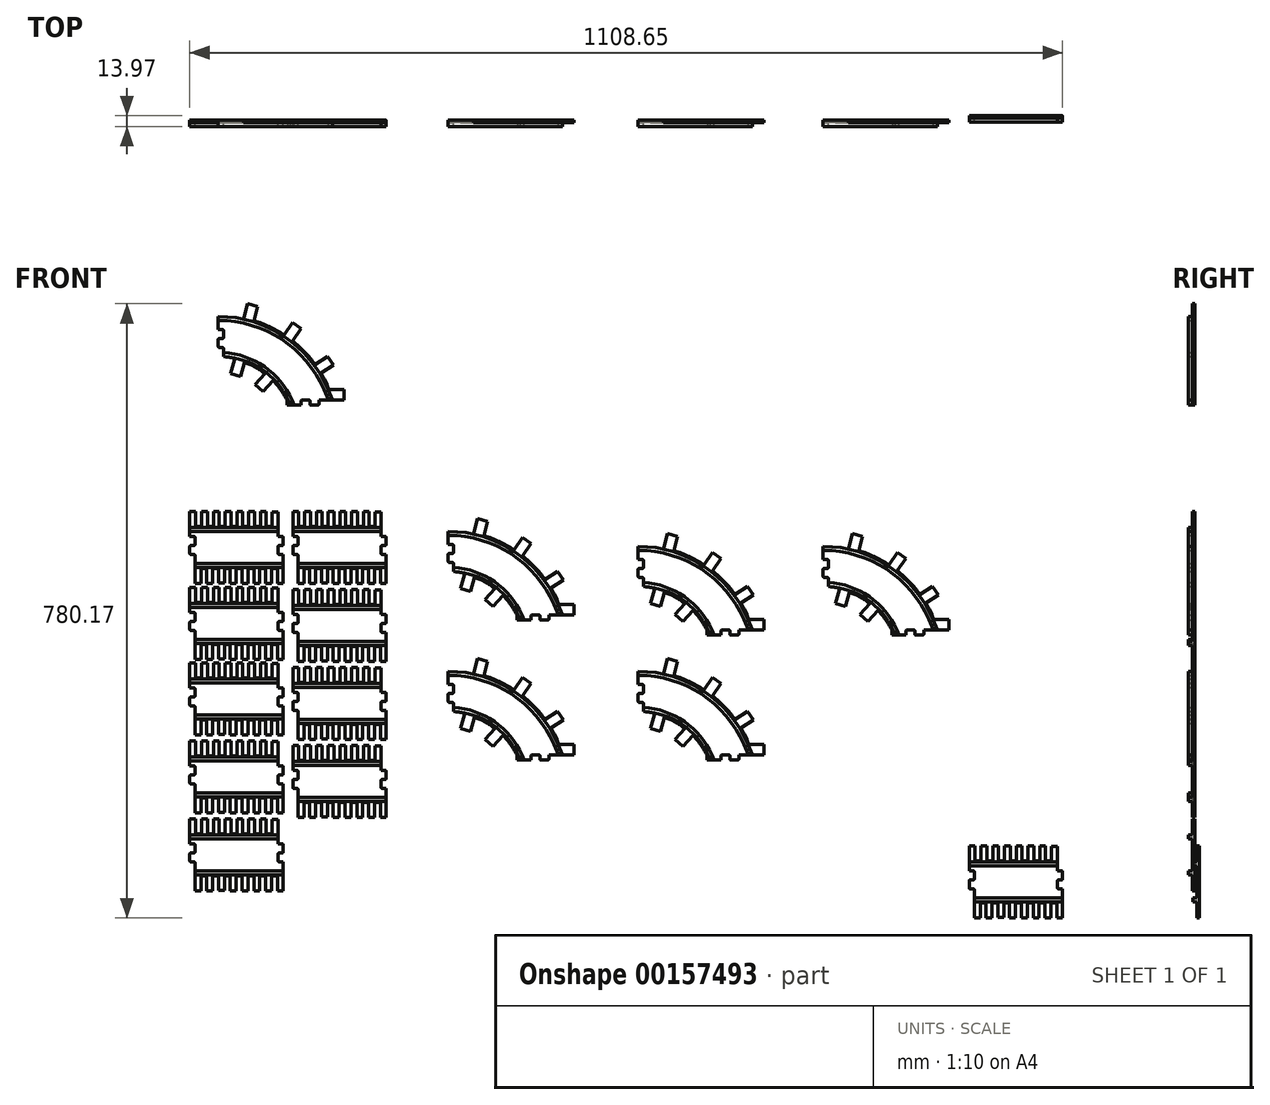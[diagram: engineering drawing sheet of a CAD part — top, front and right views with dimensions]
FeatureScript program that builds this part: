
annotation { "Feature Type Name" : "Feature", "Feature Type Description" : "" }
export const myFeature = defineFeature(function(context is Context, id is Id, definition is map)
    precondition{}
    {
        {
            var Q0;
            Q0=qCreatedBy(makeId("Front.planeOp"),FACE);
            var sketch = newSketch(context, id + "F0", { "sketchPlane" : qUnion([Q0])});
            skLineSegment(sketch, "E0.bottom", {"start": v(-84.07, 34.3) * mm, "end": v(26.8, 34.3) * mm});
            skLineSegment(sketch, "E0.top", {"start": v(-84.07, 29.2) * mm, "end": v(26.8, 29.2) * mm});
            skLineSegment(sketch, "E0.right", {"start": v(26.8, 34.29) * mm, "end": v(26.8, 29.2) * mm});
            skLineSegment(sketch, "E1", {"start": v(-78.78, 21.6) * mm, "end": v(-78.78, 12.7) * mm});
            skLineSegment(sketch, "E2", {"start": v(-80.05, 11.43) * mm, "end": v(-84.06, 11.43) * mm});
            skLineSegment(sketch, "E3", {"start": v(-85.33, 10.16) * mm, "end": v(-85.33, 1.27) * mm});
            skLineSegment(sketch, "E4", {"start": v(-84.06, 0) * mm, "end": v(-80.05, 0) * mm});
            skLineSegment(sketch, "E5", {"start": v(-78.78, -1.27) * mm, "end": v(-78.78, -11.43) * mm});
            skPoint(sketch, "E6.visualSharp", {"position": v(-78.78, 22.86) * mm});
            skArc(sketch, "E6.filletArc", {"start": v(-78.78, 21.6) * mm, "mid": v(-79.15, 22.49) * mm, "end": v(-80.05, 22.86) * mm});
            skPoint(sketch, "E7.visualSharp", {"position": v(-78.78, 11.43) * mm});
            skArc(sketch, "E7.filletArc", {"start": v(-80.05, 11.43) * mm, "mid": v(-79.15, 11.8) * mm, "end": v(-78.78, 12.7) * mm});
            skPoint(sketch, "E8.visualSharp", {"position": v(-85.33, 11.43) * mm});
            skArc(sketch, "E8.filletArc", {"start": v(-84.06, 11.43) * mm, "mid": v(-84.96, 11.06) * mm, "end": v(-85.33, 10.16) * mm});
            skPoint(sketch, "E9.visualSharp", {"position": v(-85.33, 0) * mm});
            skArc(sketch, "E9.filletArc", {"start": v(-85.33, 1.27) * mm, "mid": v(-84.96, 0.37) * mm, "end": v(-84.06, 0) * mm});
            skPoint(sketch, "E10.visualSharp", {"position": v(-78.78, 0) * mm});
            skArc(sketch, "E10.filletArc", {"start": v(-78.78, -1.27) * mm, "mid": v(-79.15, -0.37) * mm, "end": v(-80.05, 0) * mm});
            skLineSegment(sketch, "E11", {"start": v(26.8, 29.2) * mm, "end": v(26.8, 22.86) * mm});
            skLineSegment(sketch, "E12", {"start": v(26.8, 22.86) * mm, "end": v(32.09, 22.86) * mm});
            skLineSegment(sketch, "E13", {"start": v(-78.78, -11.43) * mm, "end": v(32.39, -11.43) * mm});
            skPoint(sketch, "E14.visualSharp", {"position": v(33.36, 22.86) * mm});
            skPoint(sketch, "E15.visualSharp", {"position": v(44.08, 6.35) * mm});
            skPoint(sketch, "E16.visualSharp", {"position": v(33.84, 11.43) * mm});
            skPoint(sketch, "E17.visualSharp", {"position": v(33.84, 0) * mm});
            skArc(sketch, "E17.filletArc", {"start": v(26.8, 1.27) * mm, "mid": v(27.18, 0.37) * mm, "end": v(28.07, 0) * mm});
            skLineSegment(sketch, "E18.left", {"start": v(-78.78, -11.43) * mm, "end": v(-78.78, -16.51) * mm});
            skLineSegment(sketch, "E19", {"start": v(33.36, 21.59) * mm, "end": v(33.36, 12.7) * mm});
            skLineSegment(sketch, "E20", {"start": v(32.09, 11.43) * mm, "end": v(28.07, 11.43) * mm});
            skArc(sketch, "E21.filletArc", {"start": v(33.36, 21.59) * mm, "mid": v(32.99, 22.49) * mm, "end": v(32.09, 22.86) * mm});
            skPoint(sketch, "E22.visualSharp", {"position": v(33.36, 11.43) * mm});
            skArc(sketch, "E22.filletArc", {"start": v(32.09, 11.43) * mm, "mid": v(32.99, 11.8) * mm, "end": v(33.36, 12.7) * mm});
            skLineSegment(sketch, "E23", {"start": v(26.8, 1.27) * mm, "end": v(26.8, 10.16) * mm});
            skPoint(sketch, "E24.visualSharp", {"position": v(26.8, 11.43) * mm});
            skArc(sketch, "E24.filletArc", {"start": v(28.07, 11.43) * mm, "mid": v(27.18, 11.06) * mm, "end": v(26.8, 10.16) * mm});
            skLineSegment(sketch, "E25", {"start": v(-85.34, 54.61) * mm, "end": v(-77.87, 54.61) * mm});
            skLineSegment(sketch, "E26", {"start": v(-77.87, 54.61) * mm, "end": v(-77.87, 35.74) * mm});
            skLineSegment(sketch, "E27", {"start": v(-77.87, 35.74) * mm, "end": v(-70.4, 35.74) * mm});
            skLineSegment(sketch, "E28", {"start": v(-70.4, 35.74) * mm, "end": v(-70.4, 54.6) * mm});
            skLineSegment(sketch, "E29", {"start": v(-70.4, 54.61) * mm, "end": v(-62.93, 54.61) * mm});
            skLineSegment(sketch, "E30", {"start": v(-62.93, 54.6) * mm, "end": v(-62.93, 35.74) * mm});
            skLineSegment(sketch, "E31", {"start": v(-62.93, 35.74) * mm, "end": v(-55.46, 35.74) * mm});
            skLineSegment(sketch, "E32", {"start": v(-55.46, 35.74) * mm, "end": v(-55.46, 54.6) * mm});
            skLineSegment(sketch, "E33", {"start": v(-55.46, 54.61) * mm, "end": v(-48, 54.61) * mm});
            skLineSegment(sketch, "E34", {"start": v(-48, 54.6) * mm, "end": v(-48, 35.74) * mm});
            skLineSegment(sketch, "E35", {"start": v(-48, 35.74) * mm, "end": v(-40.52, 35.74) * mm});
            skLineSegment(sketch, "E36", {"start": v(-40.52, 35.74) * mm, "end": v(-40.52, 54.6) * mm});
            skLineSegment(sketch, "E37", {"start": v(-40.52, 54.61) * mm, "end": v(-33.05, 54.61) * mm});
            skLineSegment(sketch, "E38", {"start": v(-33.05, 54.6) * mm, "end": v(-33.05, 35.74) * mm});
            skLineSegment(sketch, "E39", {"start": v(-33.05, 35.74) * mm, "end": v(-25.58, 35.74) * mm});
            skLineSegment(sketch, "E40", {"start": v(-25.58, 35.74) * mm, "end": v(-25.58, 54.6) * mm});
            skLineSegment(sketch, "E41", {"start": v(-25.58, 54.61) * mm, "end": v(-18.11, 54.61) * mm});
            skLineSegment(sketch, "E42", {"start": v(-18.11, 54.6) * mm, "end": v(-18.11, 35.74) * mm});
            skLineSegment(sketch, "E43", {"start": v(-18.11, 35.74) * mm, "end": v(-10.64, 35.74) * mm});
            skLineSegment(sketch, "E44", {"start": v(-10.64, 35.74) * mm, "end": v(-10.64, 54.6) * mm});
            skLineSegment(sketch, "E45", {"start": v(-10.64, 54.61) * mm, "end": v(-3.18, 54.61) * mm});
            skLineSegment(sketch, "E46", {"start": v(-3.18, 54.6) * mm, "end": v(-3.18, 35.74) * mm});
            skLineSegment(sketch, "E47", {"start": v(-3.18, 35.74) * mm, "end": v(4.3, 35.74) * mm});
            skLineSegment(sketch, "E48", {"start": v(4.3, 35.74) * mm, "end": v(4.3, 54.6) * mm});
            skLineSegment(sketch, "E49", {"start": v(4.3, 54.61) * mm, "end": v(11.76, 54.61) * mm});
            skLineSegment(sketch, "E50", {"start": v(11.76, 54.6) * mm, "end": v(11.76, 35.74) * mm});
            skLineSegment(sketch, "E51", {"start": v(11.76, 35.74) * mm, "end": v(19.23, 35.74) * mm});
            skLineSegment(sketch, "E52", {"start": v(19.23, 35.74) * mm, "end": v(19.23, 54.27) * mm});
            skLineSegment(sketch, "E53", {"start": v(19.23, 54.27) * mm, "end": v(26.7, 54.27) * mm});
            skLineSegment(sketch, "E54", {"start": v(26.8, 34.29) * mm, "end": v(26.7, 54.27) * mm});
            skLineSegment(sketch, "E55", {"start": v(-84.06, 22.86) * mm, "end": v(-80.05, 22.86) * mm});
            skLineSegment(sketch, "E56", {"start": v(28.07, 0) * mm, "end": v(33.36, 0) * mm});
            skLineSegment(sketch, "E57", {"start": v(33.36, 0) * mm, "end": v(33.36, -11.43) * mm});
            skLineSegment(sketch, "E58", {"start": v(32.39, -11.43) * mm, "end": v(33.36, -11.43) * mm});
            skLineSegment(sketch, "E59", {"start": v(33.36, -11.43) * mm, "end": v(33.36, -16.51) * mm});
            skLineSegment(sketch, "E60", {"start": v(-78.78, -16.51) * mm, "end": v(33.36, -16.5) * mm});
            skLineSegment(sketch, "E61", {"start": v(-78.78, 11.43) * mm, "end": v(33.84, 11.43) * mm});
            skLineSegment(sketch, "E62", {"start": v(33.36, -16.51) * mm, "end": v(33.36, -36.83) * mm});
            skLineSegment(sketch, "E63", {"start": v(33.36, -36.83) * mm, "end": v(25.89, -36.83) * mm});
            skLineSegment(sketch, "E64", {"start": v(25.89, -36.83) * mm, "end": v(25.89, -17.96) * mm});
            skLineSegment(sketch, "E65", {"start": v(25.89, -17.96) * mm, "end": v(18.42, -17.96) * mm});
            skLineSegment(sketch, "E66", {"start": v(18.42, -17.96) * mm, "end": v(18.42, -36.83) * mm});
            skLineSegment(sketch, "E67", {"start": v(18.42, -36.83) * mm, "end": v(10.95, -36.83) * mm});
            skLineSegment(sketch, "E68", {"start": v(10.95, -36.83) * mm, "end": v(10.95, -17.96) * mm});
            skLineSegment(sketch, "E69", {"start": v(10.95, -17.96) * mm, "end": v(3.48, -17.96) * mm});
            skLineSegment(sketch, "E70", {"start": v(3.48, -17.96) * mm, "end": v(3.48, -36.83) * mm});
            skLineSegment(sketch, "E71", {"start": v(3.48, -36.83) * mm, "end": v(-3.99, -36.83) * mm});
            skLineSegment(sketch, "E72", {"start": v(-3.99, -36.83) * mm, "end": v(-3.99, -17.96) * mm});
            skLineSegment(sketch, "E73", {"start": v(-3.99, -17.96) * mm, "end": v(-11.55, -17.96) * mm});
            skLineSegment(sketch, "E74", {"start": v(-11.55, -17.96) * mm, "end": v(-11.55, -36.83) * mm});
            skLineSegment(sketch, "E75", {"start": v(-11.55, -36.83) * mm, "end": v(-19.02, -36.83) * mm});
            skLineSegment(sketch, "E76", {"start": v(-19.02, -36.83) * mm, "end": v(-19.02, -17.96) * mm});
            skLineSegment(sketch, "E77", {"start": v(-19.02, -17.96) * mm, "end": v(-26.5, -17.96) * mm});
            skLineSegment(sketch, "E78", {"start": v(-26.5, -17.96) * mm, "end": v(-26.5, -36.83) * mm});
            skLineSegment(sketch, "E79", {"start": v(-26.5, -36.83) * mm, "end": v(-33.96, -36.83) * mm});
            skLineSegment(sketch, "E80", {"start": v(-33.96, -36.83) * mm, "end": v(-33.96, -17.96) * mm});
            skLineSegment(sketch, "E81", {"start": v(-33.96, -17.96) * mm, "end": v(-41.43, -17.96) * mm});
            skLineSegment(sketch, "E82", {"start": v(-41.43, -17.96) * mm, "end": v(-41.43, -36.12) * mm});
            skLineSegment(sketch, "E83", {"start": v(-41.43, -36.12) * mm, "end": v(-48.9, -36.12) * mm});
            skLineSegment(sketch, "E84", {"start": v(-48.9, -36.12) * mm, "end": v(-48.9, -17.96) * mm});
            skLineSegment(sketch, "E85", {"start": v(-48.9, -17.96) * mm, "end": v(-56.37, -17.96) * mm});
            skLineSegment(sketch, "E86", {"start": v(-56.37, -17.96) * mm, "end": v(-56.37, -36.83) * mm});
            skLineSegment(sketch, "E87", {"start": v(-56.37, -36.83) * mm, "end": v(-63.84, -36.83) * mm});
            skLineSegment(sketch, "E88", {"start": v(-63.84, -36.83) * mm, "end": v(-63.84, -17.96) * mm});
            skLineSegment(sketch, "E89", {"start": v(-63.84, -17.96) * mm, "end": v(-71.3, -17.96) * mm});
            skLineSegment(sketch, "E90", {"start": v(-71.3, -17.96) * mm, "end": v(-71.3, -36.6) * mm});
            skLineSegment(sketch, "E91", {"start": v(-71.3, -36.6) * mm, "end": v(-76.52, -36.6) * mm});
            skLineSegment(sketch, "E92", {"start": v(-78.78, -16.51) * mm, "end": v(-78.78, -36.63) * mm});
            skLineSegment(sketch, "E93", {"start": v(-78.78, -36.63) * mm, "end": v(-76.52, -36.6) * mm});
            skLineSegment(sketch, "E94", {"start": v(-84.06, 22.86) * mm, "end": v(-85.33, 22.86) * mm});
            skLineSegment(sketch, "E95", {"start": v(-85.33, 22.86) * mm, "end": v(-85.33, 22.82) * mm});
            skLineSegment(sketch, "E96", {"start": v(-85.33, 22.86) * mm, "end": v(-85.33, 29.23) * mm});
            skLineSegment(sketch, "E97", {"start": v(-84.07, 29.2) * mm, "end": v(-85.33, 29.2) * mm});
            skLineSegment(sketch, "E98", {"start": v(-85.33, 54.61) * mm, "end": v(-85.34, 54.61) * mm});
            skLineSegment(sketch, "E99", {"start": v(-85.33, 29.23) * mm, "end": v(-85.33, 54.61) * mm});
            skLineSegment(sketch, "E100", {"start": v(-84.07, 34.3) * mm, "end": v(-85.33, 34.29) * mm});
            skSolve(sketch);
        }
        {
            var Q0;
            Q0 = qSketchRegion(id + "F0", true);
            extrude(context, id + "F1", {"entities" : qUnion([Q0]), "depth" : 3.17 * mm});
        }
        {
            var Q0;
            Q0=makeQuery(id+"F1.opExtrude","CAP_FACE",FACE,{"disambiguationData":[OSD([sQuery(id+"F0.wireOp",EDGE,"E0.right"),sQuery(id+"F0.wireOp",EDGE,"E1"),sQuery(id+"F0.wireOp",EDGE,"E2"),sQuery(id+"F0.wireOp",EDGE,"E3"),sQuery(id+"F0.wireOp",EDGE,"E4"),sQuery(id+"F0.wireOp",EDGE,"E5"),sQuery(id+"F0.wireOp",EDGE,"E6.filletArc"),sQuery(id+"F0.wireOp",EDGE,"E7.filletArc"),sQuery(id+"F0.wireOp",EDGE,"E8.filletArc"),sQuery(id+"F0.wireOp",EDGE,"E9.filletArc"),sQuery(id+"F0.wireOp",EDGE,"E10.filletArc"),sQuery(id+"F0.wireOp",EDGE,"E11"),sQuery(id+"F0.wireOp",EDGE,"E17.filletArc"),sQuery(id+"F0.wireOp",EDGE,"E18.left"),sQuery(id+"F0.wireOp",EDGE,"E12"),sQuery(id+"F0.wireOp",EDGE,"E19"),sQuery(id+"F0.wireOp",EDGE,"E21.filletArc"),sQuery(id+"F0.wireOp",EDGE,"E22.filletArc"),sQuery(id+"F0.wireOp",EDGE,"E23"),sQuery(id+"F0.wireOp",EDGE,"E24.filletArc"),sQuery(id+"F0.wireOp",EDGE,"E25"),sQuery(id+"F0.wireOp",EDGE,"E26"),sQuery(id+"F0.wireOp",EDGE,"E27"),sQuery(id+"F0.wireOp",EDGE,"E28"),sQuery(id+"F0.wireOp",EDGE,"E29"),sQuery(id+"F0.wireOp",EDGE,"E30"),sQuery(id+"F0.wireOp",EDGE,"E31"),sQuery(id+"F0.wireOp",EDGE,"E32"),sQuery(id+"F0.wireOp",EDGE,"E33"),sQuery(id+"F0.wireOp",EDGE,"E34"),sQuery(id+"F0.wireOp",EDGE,"E35"),sQuery(id+"F0.wireOp",EDGE,"E36"),sQuery(id+"F0.wireOp",EDGE,"E37"),sQuery(id+"F0.wireOp",EDGE,"E38"),sQuery(id+"F0.wireOp",EDGE,"E39"),sQuery(id+"F0.wireOp",EDGE,"E40"),sQuery(id+"F0.wireOp",EDGE,"E41"),sQuery(id+"F0.wireOp",EDGE,"E42"),sQuery(id+"F0.wireOp",EDGE,"E43"),sQuery(id+"F0.wireOp",EDGE,"E44"),sQuery(id+"F0.wireOp",EDGE,"E45"),sQuery(id+"F0.wireOp",EDGE,"E46"),sQuery(id+"F0.wireOp",EDGE,"E47"),sQuery(id+"F0.wireOp",EDGE,"E48"),sQuery(id+"F0.wireOp",EDGE,"E49"),sQuery(id+"F0.wireOp",EDGE,"E50"),sQuery(id+"F0.wireOp",EDGE,"E51"),sQuery(id+"F0.wireOp",EDGE,"E52"),sQuery(id+"F0.wireOp",EDGE,"E53"),sQuery(id+"F0.wireOp",EDGE,"E54"),sQuery(id+"F0.wireOp",EDGE,"E55"),sQuery(id+"F0.wireOp",EDGE,"E56"),sQuery(id+"F0.wireOp",EDGE,"E57"),sQuery(id+"F0.wireOp",EDGE,"E59"),sQuery(id+"F0.wireOp",EDGE,"E61"),sQuery(id+"F0.wireOp",EDGE,"E62"),sQuery(id+"F0.wireOp",EDGE,"E63"),sQuery(id+"F0.wireOp",EDGE,"E64"),sQuery(id+"F0.wireOp",EDGE,"E65"),sQuery(id+"F0.wireOp",EDGE,"E66"),sQuery(id+"F0.wireOp",EDGE,"E67"),sQuery(id+"F0.wireOp",EDGE,"E68"),sQuery(id+"F0.wireOp",EDGE,"E69"),sQuery(id+"F0.wireOp",EDGE,"E70"),sQuery(id+"F0.wireOp",EDGE,"E71"),sQuery(id+"F0.wireOp",EDGE,"E72"),sQuery(id+"F0.wireOp",EDGE,"E73"),sQuery(id+"F0.wireOp",EDGE,"E74"),sQuery(id+"F0.wireOp",EDGE,"E75"),sQuery(id+"F0.wireOp",EDGE,"E76"),sQuery(id+"F0.wireOp",EDGE,"E77"),sQuery(id+"F0.wireOp",EDGE,"E78"),sQuery(id+"F0.wireOp",EDGE,"E79"),sQuery(id+"F0.wireOp",EDGE,"E80"),sQuery(id+"F0.wireOp",EDGE,"E81"),sQuery(id+"F0.wireOp",EDGE,"E82"),sQuery(id+"F0.wireOp",EDGE,"E83"),sQuery(id+"F0.wireOp",EDGE,"E84"),sQuery(id+"F0.wireOp",EDGE,"E85"),sQuery(id+"F0.wireOp",EDGE,"E86"),sQuery(id+"F0.wireOp",EDGE,"E87"),sQuery(id+"F0.wireOp",EDGE,"E88"),sQuery(id+"F0.wireOp",EDGE,"E89"),sQuery(id+"F0.wireOp",EDGE,"E90"),sQuery(id+"F0.wireOp",EDGE,"E91"),sQuery(id+"F0.wireOp",EDGE,"E92"),sQuery(id+"F0.wireOp",EDGE,"E93"),sQuery(id+"F0.wireOp",EDGE,"E94"),sQuery(id+"F0.wireOp",EDGE,"E96"),sQuery(id+"F0.wireOp",EDGE,"E99")])],"isStart":false});
            var sketch = newSketch(context, id + "F2", { "sketchPlane" : qUnion([Q0])});
            skLineSegment(sketch, "E101.0.0", {"start": v(26.8, 34.3) * mm, "end": v(-84.07, 34.3) * mm});
            skLineSegment(sketch, "E101.0.1", {"start": v(-84.07, 34.3) * mm, "end": v(-85.33, 34.29) * mm});
            skLineSegment(sketch, "E101.0.2", {"start": v(-85.33, 34.29) * mm, "end": v(-85.33, 29.23) * mm});
            skLineSegment(sketch, "E101.0.3", {"start": v(-85.33, 29.23) * mm, "end": v(-85.33, 29.2) * mm});
            skLineSegment(sketch, "E101.0.4", {"start": v(-85.33, 29.2) * mm, "end": v(-84.07, 29.2) * mm});
            skLineSegment(sketch, "E101.0.5", {"start": v(-84.07, 29.2) * mm, "end": v(26.8, 29.2) * mm});
            skLineSegment(sketch, "E101.0.6", {"start": v(26.8, 29.2) * mm, "end": v(26.8, 34.29) * mm});
            skLineSegment(sketch, "E102.0.0", {"start": v(32.39, -11.43) * mm, "end": v(-78.78, -11.43) * mm});
            skLineSegment(sketch, "E102.0.1", {"start": v(-78.78, -11.43) * mm, "end": v(-78.78, -16.51) * mm});
            skLineSegment(sketch, "E102.0.2", {"start": v(-78.78, -16.51) * mm, "end": v(33.36, -16.5) * mm});
            skLineSegment(sketch, "E102.0.3", {"start": v(33.36, -16.51) * mm, "end": v(33.36, -11.43) * mm});
            skLineSegment(sketch, "E102.0.4", {"start": v(33.36, -11.43) * mm, "end": v(32.39, -11.43) * mm});
            skSolve(sketch);
        }
        {
            var Q0;
            Q0 = qSketchRegion(id + "F2", true);
            extrude(context, id + "F3", {"entities" : qUnion([Q0]), "operationType" : NewBodyOperationType.ADD, "depth" : 5.08 * mm});
        }
        {
            var Q0;
            Q0 = qSketchRegion(id + "F2", true);
            extrude(context, id + "F4", {"entities" : qUnion([Q0]), "operationType" : NewBodyOperationType.ADD, "depth" : 5.08 * mm});
        }
        {
            var Q0;
            Q0=makeQuery(id+"F1.opExtrude","SWEPT_BODY",BODY,{"disambiguationData":[OSD([sQuery(id+"F0.wireOp",EDGE,"E0.right"),sQuery(id+"F0.wireOp",EDGE,"E1"),sQuery(id+"F0.wireOp",EDGE,"E2"),sQuery(id+"F0.wireOp",EDGE,"E3"),sQuery(id+"F0.wireOp",EDGE,"E4"),sQuery(id+"F0.wireOp",EDGE,"E5"),sQuery(id+"F0.wireOp",EDGE,"E6.filletArc"),sQuery(id+"F0.wireOp",EDGE,"E7.filletArc"),sQuery(id+"F0.wireOp",EDGE,"E8.filletArc"),sQuery(id+"F0.wireOp",EDGE,"E9.filletArc"),sQuery(id+"F0.wireOp",EDGE,"E10.filletArc"),sQuery(id+"F0.wireOp",EDGE,"E11"),sQuery(id+"F0.wireOp",EDGE,"E17.filletArc"),sQuery(id+"F0.wireOp",EDGE,"E18.left"),sQuery(id+"F0.wireOp",EDGE,"E12"),sQuery(id+"F0.wireOp",EDGE,"E19"),sQuery(id+"F0.wireOp",EDGE,"E21.filletArc"),sQuery(id+"F0.wireOp",EDGE,"E22.filletArc"),sQuery(id+"F0.wireOp",EDGE,"E23"),sQuery(id+"F0.wireOp",EDGE,"E24.filletArc"),sQuery(id+"F0.wireOp",EDGE,"E25"),sQuery(id+"F0.wireOp",EDGE,"E26"),sQuery(id+"F0.wireOp",EDGE,"E27"),sQuery(id+"F0.wireOp",EDGE,"E28"),sQuery(id+"F0.wireOp",EDGE,"E29"),sQuery(id+"F0.wireOp",EDGE,"E30"),sQuery(id+"F0.wireOp",EDGE,"E31"),sQuery(id+"F0.wireOp",EDGE,"E32"),sQuery(id+"F0.wireOp",EDGE,"E33"),sQuery(id+"F0.wireOp",EDGE,"E34"),sQuery(id+"F0.wireOp",EDGE,"E35"),sQuery(id+"F0.wireOp",EDGE,"E36"),sQuery(id+"F0.wireOp",EDGE,"E37"),sQuery(id+"F0.wireOp",EDGE,"E38"),sQuery(id+"F0.wireOp",EDGE,"E39"),sQuery(id+"F0.wireOp",EDGE,"E40"),sQuery(id+"F0.wireOp",EDGE,"E41"),sQuery(id+"F0.wireOp",EDGE,"E42"),sQuery(id+"F0.wireOp",EDGE,"E43"),sQuery(id+"F0.wireOp",EDGE,"E44"),sQuery(id+"F0.wireOp",EDGE,"E45"),sQuery(id+"F0.wireOp",EDGE,"E46"),sQuery(id+"F0.wireOp",EDGE,"E47"),sQuery(id+"F0.wireOp",EDGE,"E48"),sQuery(id+"F0.wireOp",EDGE,"E49"),sQuery(id+"F0.wireOp",EDGE,"E50"),sQuery(id+"F0.wireOp",EDGE,"E51"),sQuery(id+"F0.wireOp",EDGE,"E52"),sQuery(id+"F0.wireOp",EDGE,"E53"),sQuery(id+"F0.wireOp",EDGE,"E54"),sQuery(id+"F0.wireOp",EDGE,"E55"),sQuery(id+"F0.wireOp",EDGE,"E56"),sQuery(id+"F0.wireOp",EDGE,"E57"),sQuery(id+"F0.wireOp",EDGE,"E59"),sQuery(id+"F0.wireOp",EDGE,"E61"),sQuery(id+"F0.wireOp",EDGE,"E62"),sQuery(id+"F0.wireOp",EDGE,"E63"),sQuery(id+"F0.wireOp",EDGE,"E64"),sQuery(id+"F0.wireOp",EDGE,"E65"),sQuery(id+"F0.wireOp",EDGE,"E66"),sQuery(id+"F0.wireOp",EDGE,"E67"),sQuery(id+"F0.wireOp",EDGE,"E68"),sQuery(id+"F0.wireOp",EDGE,"E69"),sQuery(id+"F0.wireOp",EDGE,"E70"),sQuery(id+"F0.wireOp",EDGE,"E71"),sQuery(id+"F0.wireOp",EDGE,"E72"),sQuery(id+"F0.wireOp",EDGE,"E73"),sQuery(id+"F0.wireOp",EDGE,"E74"),sQuery(id+"F0.wireOp",EDGE,"E75"),sQuery(id+"F0.wireOp",EDGE,"E76"),sQuery(id+"F0.wireOp",EDGE,"E77"),sQuery(id+"F0.wireOp",EDGE,"E78"),sQuery(id+"F0.wireOp",EDGE,"E79"),sQuery(id+"F0.wireOp",EDGE,"E80"),sQuery(id+"F0.wireOp",EDGE,"E81"),sQuery(id+"F0.wireOp",EDGE,"E82"),sQuery(id+"F0.wireOp",EDGE,"E83"),sQuery(id+"F0.wireOp",EDGE,"E84"),sQuery(id+"F0.wireOp",EDGE,"E85"),sQuery(id+"F0.wireOp",EDGE,"E86"),sQuery(id+"F0.wireOp",EDGE,"E87"),sQuery(id+"F0.wireOp",EDGE,"E88"),sQuery(id+"F0.wireOp",EDGE,"E89"),sQuery(id+"F0.wireOp",EDGE,"E90"),sQuery(id+"F0.wireOp",EDGE,"E91"),sQuery(id+"F0.wireOp",EDGE,"E92"),sQuery(id+"F0.wireOp",EDGE,"E93"),sQuery(id+"F0.wireOp",EDGE,"E94"),sQuery(id+"F0.wireOp",EDGE,"E96"),sQuery(id+"F0.wireOp",EDGE,"E99")])]});
            transform(context, id + "F5", {"entities" : qUnion([Q0]), "transformType" : TransformType.TRANSLATION_3D, "dx" : 0 * mm, "dy" : 0 * mm, "dz" : 0 * mm, "makeCopy" : true});
        }
        {
            var Q0;
            Q0=makeQuery(id+"F5.opPattern","COPY",BODY,{"derivedFrom":makeQuery(id+"F1.opExtrude","SWEPT_BODY",BODY,{"disambiguationData":[OSD([sQuery(id+"F0.wireOp",EDGE,"E0.right"),sQuery(id+"F0.wireOp",EDGE,"E1"),sQuery(id+"F0.wireOp",EDGE,"E2"),sQuery(id+"F0.wireOp",EDGE,"E3"),sQuery(id+"F0.wireOp",EDGE,"E4"),sQuery(id+"F0.wireOp",EDGE,"E5"),sQuery(id+"F0.wireOp",EDGE,"E6.filletArc"),sQuery(id+"F0.wireOp",EDGE,"E7.filletArc"),sQuery(id+"F0.wireOp",EDGE,"E8.filletArc"),sQuery(id+"F0.wireOp",EDGE,"E9.filletArc"),sQuery(id+"F0.wireOp",EDGE,"E10.filletArc"),sQuery(id+"F0.wireOp",EDGE,"E11"),sQuery(id+"F0.wireOp",EDGE,"E17.filletArc"),sQuery(id+"F0.wireOp",EDGE,"E18.left"),sQuery(id+"F0.wireOp",EDGE,"E12"),sQuery(id+"F0.wireOp",EDGE,"E19"),sQuery(id+"F0.wireOp",EDGE,"E21.filletArc"),sQuery(id+"F0.wireOp",EDGE,"E22.filletArc"),sQuery(id+"F0.wireOp",EDGE,"E23"),sQuery(id+"F0.wireOp",EDGE,"E24.filletArc"),sQuery(id+"F0.wireOp",EDGE,"E25"),sQuery(id+"F0.wireOp",EDGE,"E26"),sQuery(id+"F0.wireOp",EDGE,"E27"),sQuery(id+"F0.wireOp",EDGE,"E28"),sQuery(id+"F0.wireOp",EDGE,"E29"),sQuery(id+"F0.wireOp",EDGE,"E30"),sQuery(id+"F0.wireOp",EDGE,"E31"),sQuery(id+"F0.wireOp",EDGE,"E32"),sQuery(id+"F0.wireOp",EDGE,"E33"),sQuery(id+"F0.wireOp",EDGE,"E34"),sQuery(id+"F0.wireOp",EDGE,"E35"),sQuery(id+"F0.wireOp",EDGE,"E36"),sQuery(id+"F0.wireOp",EDGE,"E37"),sQuery(id+"F0.wireOp",EDGE,"E38"),sQuery(id+"F0.wireOp",EDGE,"E39"),sQuery(id+"F0.wireOp",EDGE,"E40"),sQuery(id+"F0.wireOp",EDGE,"E41"),sQuery(id+"F0.wireOp",EDGE,"E42"),sQuery(id+"F0.wireOp",EDGE,"E43"),sQuery(id+"F0.wireOp",EDGE,"E44"),sQuery(id+"F0.wireOp",EDGE,"E45"),sQuery(id+"F0.wireOp",EDGE,"E46"),sQuery(id+"F0.wireOp",EDGE,"E47"),sQuery(id+"F0.wireOp",EDGE,"E48"),sQuery(id+"F0.wireOp",EDGE,"E49"),sQuery(id+"F0.wireOp",EDGE,"E50"),sQuery(id+"F0.wireOp",EDGE,"E51"),sQuery(id+"F0.wireOp",EDGE,"E52"),sQuery(id+"F0.wireOp",EDGE,"E53"),sQuery(id+"F0.wireOp",EDGE,"E54"),sQuery(id+"F0.wireOp",EDGE,"E55"),sQuery(id+"F0.wireOp",EDGE,"E56"),sQuery(id+"F0.wireOp",EDGE,"E57"),sQuery(id+"F0.wireOp",EDGE,"E59"),sQuery(id+"F0.wireOp",EDGE,"E61"),sQuery(id+"F0.wireOp",EDGE,"E62"),sQuery(id+"F0.wireOp",EDGE,"E63"),sQuery(id+"F0.wireOp",EDGE,"E64"),sQuery(id+"F0.wireOp",EDGE,"E65"),sQuery(id+"F0.wireOp",EDGE,"E66"),sQuery(id+"F0.wireOp",EDGE,"E67"),sQuery(id+"F0.wireOp",EDGE,"E68"),sQuery(id+"F0.wireOp",EDGE,"E69"),sQuery(id+"F0.wireOp",EDGE,"E70"),sQuery(id+"F0.wireOp",EDGE,"E71"),sQuery(id+"F0.wireOp",EDGE,"E72"),sQuery(id+"F0.wireOp",EDGE,"E73"),sQuery(id+"F0.wireOp",EDGE,"E74"),sQuery(id+"F0.wireOp",EDGE,"E75"),sQuery(id+"F0.wireOp",EDGE,"E76"),sQuery(id+"F0.wireOp",EDGE,"E77"),sQuery(id+"F0.wireOp",EDGE,"E78"),sQuery(id+"F0.wireOp",EDGE,"E79"),sQuery(id+"F0.wireOp",EDGE,"E80"),sQuery(id+"F0.wireOp",EDGE,"E81"),sQuery(id+"F0.wireOp",EDGE,"E82"),sQuery(id+"F0.wireOp",EDGE,"E83"),sQuery(id+"F0.wireOp",EDGE,"E84"),sQuery(id+"F0.wireOp",EDGE,"E85"),sQuery(id+"F0.wireOp",EDGE,"E86"),sQuery(id+"F0.wireOp",EDGE,"E87"),sQuery(id+"F0.wireOp",EDGE,"E88"),sQuery(id+"F0.wireOp",EDGE,"E89"),sQuery(id+"F0.wireOp",EDGE,"E90"),sQuery(id+"F0.wireOp",EDGE,"E91"),sQuery(id+"F0.wireOp",EDGE,"E92"),sQuery(id+"F0.wireOp",EDGE,"E93"),sQuery(id+"F0.wireOp",EDGE,"E94"),sQuery(id+"F0.wireOp",EDGE,"E96"),sQuery(id+"F0.wireOp",EDGE,"E99")])]}),"instanceName":"1"});
            deleteBodies(context, id + "F6", {"entities" : qUnion([Q0])});
        }
        {
            var Q0;
            Q0=makeQuery(id+"F1.opExtrude","SWEPT_BODY",BODY,{"disambiguationData":[OSD([sQuery(id+"F0.wireOp",EDGE,"E0.right"),sQuery(id+"F0.wireOp",EDGE,"E1"),sQuery(id+"F0.wireOp",EDGE,"E2"),sQuery(id+"F0.wireOp",EDGE,"E3"),sQuery(id+"F0.wireOp",EDGE,"E4"),sQuery(id+"F0.wireOp",EDGE,"E5"),sQuery(id+"F0.wireOp",EDGE,"E6.filletArc"),sQuery(id+"F0.wireOp",EDGE,"E7.filletArc"),sQuery(id+"F0.wireOp",EDGE,"E8.filletArc"),sQuery(id+"F0.wireOp",EDGE,"E9.filletArc"),sQuery(id+"F0.wireOp",EDGE,"E10.filletArc"),sQuery(id+"F0.wireOp",EDGE,"E11"),sQuery(id+"F0.wireOp",EDGE,"E17.filletArc"),sQuery(id+"F0.wireOp",EDGE,"E18.left"),sQuery(id+"F0.wireOp",EDGE,"E12"),sQuery(id+"F0.wireOp",EDGE,"E19"),sQuery(id+"F0.wireOp",EDGE,"E21.filletArc"),sQuery(id+"F0.wireOp",EDGE,"E22.filletArc"),sQuery(id+"F0.wireOp",EDGE,"E23"),sQuery(id+"F0.wireOp",EDGE,"E24.filletArc"),sQuery(id+"F0.wireOp",EDGE,"E25"),sQuery(id+"F0.wireOp",EDGE,"E26"),sQuery(id+"F0.wireOp",EDGE,"E27"),sQuery(id+"F0.wireOp",EDGE,"E28"),sQuery(id+"F0.wireOp",EDGE,"E29"),sQuery(id+"F0.wireOp",EDGE,"E30"),sQuery(id+"F0.wireOp",EDGE,"E31"),sQuery(id+"F0.wireOp",EDGE,"E32"),sQuery(id+"F0.wireOp",EDGE,"E33"),sQuery(id+"F0.wireOp",EDGE,"E34"),sQuery(id+"F0.wireOp",EDGE,"E35"),sQuery(id+"F0.wireOp",EDGE,"E36"),sQuery(id+"F0.wireOp",EDGE,"E37"),sQuery(id+"F0.wireOp",EDGE,"E38"),sQuery(id+"F0.wireOp",EDGE,"E39"),sQuery(id+"F0.wireOp",EDGE,"E40"),sQuery(id+"F0.wireOp",EDGE,"E41"),sQuery(id+"F0.wireOp",EDGE,"E42"),sQuery(id+"F0.wireOp",EDGE,"E43"),sQuery(id+"F0.wireOp",EDGE,"E44"),sQuery(id+"F0.wireOp",EDGE,"E45"),sQuery(id+"F0.wireOp",EDGE,"E46"),sQuery(id+"F0.wireOp",EDGE,"E47"),sQuery(id+"F0.wireOp",EDGE,"E48"),sQuery(id+"F0.wireOp",EDGE,"E49"),sQuery(id+"F0.wireOp",EDGE,"E50"),sQuery(id+"F0.wireOp",EDGE,"E51"),sQuery(id+"F0.wireOp",EDGE,"E52"),sQuery(id+"F0.wireOp",EDGE,"E53"),sQuery(id+"F0.wireOp",EDGE,"E54"),sQuery(id+"F0.wireOp",EDGE,"E55"),sQuery(id+"F0.wireOp",EDGE,"E56"),sQuery(id+"F0.wireOp",EDGE,"E57"),sQuery(id+"F0.wireOp",EDGE,"E59"),sQuery(id+"F0.wireOp",EDGE,"E61"),sQuery(id+"F0.wireOp",EDGE,"E62"),sQuery(id+"F0.wireOp",EDGE,"E63"),sQuery(id+"F0.wireOp",EDGE,"E64"),sQuery(id+"F0.wireOp",EDGE,"E65"),sQuery(id+"F0.wireOp",EDGE,"E66"),sQuery(id+"F0.wireOp",EDGE,"E67"),sQuery(id+"F0.wireOp",EDGE,"E68"),sQuery(id+"F0.wireOp",EDGE,"E69"),sQuery(id+"F0.wireOp",EDGE,"E70"),sQuery(id+"F0.wireOp",EDGE,"E71"),sQuery(id+"F0.wireOp",EDGE,"E72"),sQuery(id+"F0.wireOp",EDGE,"E73"),sQuery(id+"F0.wireOp",EDGE,"E74"),sQuery(id+"F0.wireOp",EDGE,"E75"),sQuery(id+"F0.wireOp",EDGE,"E76"),sQuery(id+"F0.wireOp",EDGE,"E77"),sQuery(id+"F0.wireOp",EDGE,"E78"),sQuery(id+"F0.wireOp",EDGE,"E79"),sQuery(id+"F0.wireOp",EDGE,"E80"),sQuery(id+"F0.wireOp",EDGE,"E81"),sQuery(id+"F0.wireOp",EDGE,"E82"),sQuery(id+"F0.wireOp",EDGE,"E83"),sQuery(id+"F0.wireOp",EDGE,"E84"),sQuery(id+"F0.wireOp",EDGE,"E85"),sQuery(id+"F0.wireOp",EDGE,"E86"),sQuery(id+"F0.wireOp",EDGE,"E87"),sQuery(id+"F0.wireOp",EDGE,"E88"),sQuery(id+"F0.wireOp",EDGE,"E89"),sQuery(id+"F0.wireOp",EDGE,"E90"),sQuery(id+"F0.wireOp",EDGE,"E91"),sQuery(id+"F0.wireOp",EDGE,"E92"),sQuery(id+"F0.wireOp",EDGE,"E93"),sQuery(id+"F0.wireOp",EDGE,"E94"),sQuery(id+"F0.wireOp",EDGE,"E96"),sQuery(id+"F0.wireOp",EDGE,"E99")])]});
            transform(context, id + "F7", {"entities" : qUnion([Q0]), "transformType" : TransformType.TRANSLATION_3D, "dx" : 0 * mm, "dy" : 0 * mm, "dz" : -96.52 * mm, "makeCopy" : true});
        }
        {
            var Q0;
            Q0=makeQuery(id+"F7.opPattern","COPY",BODY,{"derivedFrom":makeQuery(id+"F1.opExtrude","SWEPT_BODY",BODY,{"disambiguationData":[OSD([sQuery(id+"F0.wireOp",EDGE,"E0.right"),sQuery(id+"F0.wireOp",EDGE,"E1"),sQuery(id+"F0.wireOp",EDGE,"E2"),sQuery(id+"F0.wireOp",EDGE,"E3"),sQuery(id+"F0.wireOp",EDGE,"E4"),sQuery(id+"F0.wireOp",EDGE,"E5"),sQuery(id+"F0.wireOp",EDGE,"E6.filletArc"),sQuery(id+"F0.wireOp",EDGE,"E7.filletArc"),sQuery(id+"F0.wireOp",EDGE,"E8.filletArc"),sQuery(id+"F0.wireOp",EDGE,"E9.filletArc"),sQuery(id+"F0.wireOp",EDGE,"E10.filletArc"),sQuery(id+"F0.wireOp",EDGE,"E11"),sQuery(id+"F0.wireOp",EDGE,"E17.filletArc"),sQuery(id+"F0.wireOp",EDGE,"E18.left"),sQuery(id+"F0.wireOp",EDGE,"E12"),sQuery(id+"F0.wireOp",EDGE,"E19"),sQuery(id+"F0.wireOp",EDGE,"E21.filletArc"),sQuery(id+"F0.wireOp",EDGE,"E22.filletArc"),sQuery(id+"F0.wireOp",EDGE,"E23"),sQuery(id+"F0.wireOp",EDGE,"E24.filletArc"),sQuery(id+"F0.wireOp",EDGE,"E25"),sQuery(id+"F0.wireOp",EDGE,"E26"),sQuery(id+"F0.wireOp",EDGE,"E27"),sQuery(id+"F0.wireOp",EDGE,"E28"),sQuery(id+"F0.wireOp",EDGE,"E29"),sQuery(id+"F0.wireOp",EDGE,"E30"),sQuery(id+"F0.wireOp",EDGE,"E31"),sQuery(id+"F0.wireOp",EDGE,"E32"),sQuery(id+"F0.wireOp",EDGE,"E33"),sQuery(id+"F0.wireOp",EDGE,"E34"),sQuery(id+"F0.wireOp",EDGE,"E35"),sQuery(id+"F0.wireOp",EDGE,"E36"),sQuery(id+"F0.wireOp",EDGE,"E37"),sQuery(id+"F0.wireOp",EDGE,"E38"),sQuery(id+"F0.wireOp",EDGE,"E39"),sQuery(id+"F0.wireOp",EDGE,"E40"),sQuery(id+"F0.wireOp",EDGE,"E41"),sQuery(id+"F0.wireOp",EDGE,"E42"),sQuery(id+"F0.wireOp",EDGE,"E43"),sQuery(id+"F0.wireOp",EDGE,"E44"),sQuery(id+"F0.wireOp",EDGE,"E45"),sQuery(id+"F0.wireOp",EDGE,"E46"),sQuery(id+"F0.wireOp",EDGE,"E47"),sQuery(id+"F0.wireOp",EDGE,"E48"),sQuery(id+"F0.wireOp",EDGE,"E49"),sQuery(id+"F0.wireOp",EDGE,"E50"),sQuery(id+"F0.wireOp",EDGE,"E51"),sQuery(id+"F0.wireOp",EDGE,"E52"),sQuery(id+"F0.wireOp",EDGE,"E53"),sQuery(id+"F0.wireOp",EDGE,"E54"),sQuery(id+"F0.wireOp",EDGE,"E55"),sQuery(id+"F0.wireOp",EDGE,"E56"),sQuery(id+"F0.wireOp",EDGE,"E57"),sQuery(id+"F0.wireOp",EDGE,"E59"),sQuery(id+"F0.wireOp",EDGE,"E61"),sQuery(id+"F0.wireOp",EDGE,"E62"),sQuery(id+"F0.wireOp",EDGE,"E63"),sQuery(id+"F0.wireOp",EDGE,"E64"),sQuery(id+"F0.wireOp",EDGE,"E65"),sQuery(id+"F0.wireOp",EDGE,"E66"),sQuery(id+"F0.wireOp",EDGE,"E67"),sQuery(id+"F0.wireOp",EDGE,"E68"),sQuery(id+"F0.wireOp",EDGE,"E69"),sQuery(id+"F0.wireOp",EDGE,"E70"),sQuery(id+"F0.wireOp",EDGE,"E71"),sQuery(id+"F0.wireOp",EDGE,"E72"),sQuery(id+"F0.wireOp",EDGE,"E73"),sQuery(id+"F0.wireOp",EDGE,"E74"),sQuery(id+"F0.wireOp",EDGE,"E75"),sQuery(id+"F0.wireOp",EDGE,"E76"),sQuery(id+"F0.wireOp",EDGE,"E77"),sQuery(id+"F0.wireOp",EDGE,"E78"),sQuery(id+"F0.wireOp",EDGE,"E79"),sQuery(id+"F0.wireOp",EDGE,"E80"),sQuery(id+"F0.wireOp",EDGE,"E81"),sQuery(id+"F0.wireOp",EDGE,"E82"),sQuery(id+"F0.wireOp",EDGE,"E83"),sQuery(id+"F0.wireOp",EDGE,"E84"),sQuery(id+"F0.wireOp",EDGE,"E85"),sQuery(id+"F0.wireOp",EDGE,"E86"),sQuery(id+"F0.wireOp",EDGE,"E87"),sQuery(id+"F0.wireOp",EDGE,"E88"),sQuery(id+"F0.wireOp",EDGE,"E89"),sQuery(id+"F0.wireOp",EDGE,"E90"),sQuery(id+"F0.wireOp",EDGE,"E91"),sQuery(id+"F0.wireOp",EDGE,"E92"),sQuery(id+"F0.wireOp",EDGE,"E93"),sQuery(id+"F0.wireOp",EDGE,"E94"),sQuery(id+"F0.wireOp",EDGE,"E96"),sQuery(id+"F0.wireOp",EDGE,"E99")])]}),"instanceName":"1"});
            transform(context, id + "F8", {"entities" : qUnion([Q0]), "transformType" : TransformType.TRANSLATION_3D, "dx" : 0 * mm, "dy" : 0 * mm, "dz" : -95.88 * mm, "makeCopy" : true});
        }
        {
            var Q0;
            Q0=makeQuery(id+"F8.opPattern","COPY",BODY,{"derivedFrom":makeQuery(id+"F7.opPattern","COPY",BODY,{"derivedFrom":makeQuery(id+"F1.opExtrude","SWEPT_BODY",BODY,{"disambiguationData":[OSD([sQuery(id+"F0.wireOp",EDGE,"E0.right"),sQuery(id+"F0.wireOp",EDGE,"E1"),sQuery(id+"F0.wireOp",EDGE,"E2"),sQuery(id+"F0.wireOp",EDGE,"E3"),sQuery(id+"F0.wireOp",EDGE,"E4"),sQuery(id+"F0.wireOp",EDGE,"E5"),sQuery(id+"F0.wireOp",EDGE,"E6.filletArc"),sQuery(id+"F0.wireOp",EDGE,"E7.filletArc"),sQuery(id+"F0.wireOp",EDGE,"E8.filletArc"),sQuery(id+"F0.wireOp",EDGE,"E9.filletArc"),sQuery(id+"F0.wireOp",EDGE,"E10.filletArc"),sQuery(id+"F0.wireOp",EDGE,"E11"),sQuery(id+"F0.wireOp",EDGE,"E17.filletArc"),sQuery(id+"F0.wireOp",EDGE,"E18.left"),sQuery(id+"F0.wireOp",EDGE,"E12"),sQuery(id+"F0.wireOp",EDGE,"E19"),sQuery(id+"F0.wireOp",EDGE,"E21.filletArc"),sQuery(id+"F0.wireOp",EDGE,"E22.filletArc"),sQuery(id+"F0.wireOp",EDGE,"E23"),sQuery(id+"F0.wireOp",EDGE,"E24.filletArc"),sQuery(id+"F0.wireOp",EDGE,"E25"),sQuery(id+"F0.wireOp",EDGE,"E26"),sQuery(id+"F0.wireOp",EDGE,"E27"),sQuery(id+"F0.wireOp",EDGE,"E28"),sQuery(id+"F0.wireOp",EDGE,"E29"),sQuery(id+"F0.wireOp",EDGE,"E30"),sQuery(id+"F0.wireOp",EDGE,"E31"),sQuery(id+"F0.wireOp",EDGE,"E32"),sQuery(id+"F0.wireOp",EDGE,"E33"),sQuery(id+"F0.wireOp",EDGE,"E34"),sQuery(id+"F0.wireOp",EDGE,"E35"),sQuery(id+"F0.wireOp",EDGE,"E36"),sQuery(id+"F0.wireOp",EDGE,"E37"),sQuery(id+"F0.wireOp",EDGE,"E38"),sQuery(id+"F0.wireOp",EDGE,"E39"),sQuery(id+"F0.wireOp",EDGE,"E40"),sQuery(id+"F0.wireOp",EDGE,"E41"),sQuery(id+"F0.wireOp",EDGE,"E42"),sQuery(id+"F0.wireOp",EDGE,"E43"),sQuery(id+"F0.wireOp",EDGE,"E44"),sQuery(id+"F0.wireOp",EDGE,"E45"),sQuery(id+"F0.wireOp",EDGE,"E46"),sQuery(id+"F0.wireOp",EDGE,"E47"),sQuery(id+"F0.wireOp",EDGE,"E48"),sQuery(id+"F0.wireOp",EDGE,"E49"),sQuery(id+"F0.wireOp",EDGE,"E50"),sQuery(id+"F0.wireOp",EDGE,"E51"),sQuery(id+"F0.wireOp",EDGE,"E52"),sQuery(id+"F0.wireOp",EDGE,"E53"),sQuery(id+"F0.wireOp",EDGE,"E54"),sQuery(id+"F0.wireOp",EDGE,"E55"),sQuery(id+"F0.wireOp",EDGE,"E56"),sQuery(id+"F0.wireOp",EDGE,"E57"),sQuery(id+"F0.wireOp",EDGE,"E59"),sQuery(id+"F0.wireOp",EDGE,"E61"),sQuery(id+"F0.wireOp",EDGE,"E62"),sQuery(id+"F0.wireOp",EDGE,"E63"),sQuery(id+"F0.wireOp",EDGE,"E64"),sQuery(id+"F0.wireOp",EDGE,"E65"),sQuery(id+"F0.wireOp",EDGE,"E66"),sQuery(id+"F0.wireOp",EDGE,"E67"),sQuery(id+"F0.wireOp",EDGE,"E68"),sQuery(id+"F0.wireOp",EDGE,"E69"),sQuery(id+"F0.wireOp",EDGE,"E70"),sQuery(id+"F0.wireOp",EDGE,"E71"),sQuery(id+"F0.wireOp",EDGE,"E72"),sQuery(id+"F0.wireOp",EDGE,"E73"),sQuery(id+"F0.wireOp",EDGE,"E74"),sQuery(id+"F0.wireOp",EDGE,"E75"),sQuery(id+"F0.wireOp",EDGE,"E76"),sQuery(id+"F0.wireOp",EDGE,"E77"),sQuery(id+"F0.wireOp",EDGE,"E78"),sQuery(id+"F0.wireOp",EDGE,"E79"),sQuery(id+"F0.wireOp",EDGE,"E80"),sQuery(id+"F0.wireOp",EDGE,"E81"),sQuery(id+"F0.wireOp",EDGE,"E82"),sQuery(id+"F0.wireOp",EDGE,"E83"),sQuery(id+"F0.wireOp",EDGE,"E84"),sQuery(id+"F0.wireOp",EDGE,"E85"),sQuery(id+"F0.wireOp",EDGE,"E86"),sQuery(id+"F0.wireOp",EDGE,"E87"),sQuery(id+"F0.wireOp",EDGE,"E88"),sQuery(id+"F0.wireOp",EDGE,"E89"),sQuery(id+"F0.wireOp",EDGE,"E90"),sQuery(id+"F0.wireOp",EDGE,"E91"),sQuery(id+"F0.wireOp",EDGE,"E92"),sQuery(id+"F0.wireOp",EDGE,"E93"),sQuery(id+"F0.wireOp",EDGE,"E94"),sQuery(id+"F0.wireOp",EDGE,"E96"),sQuery(id+"F0.wireOp",EDGE,"E99")])]}),"instanceName":"1"}),"instanceName":"1"});
            transform(context, id + "F9", {"entities" : qUnion([Q0]), "transformType" : TransformType.TRANSLATION_3D, "dx" : 0 * mm, "dy" : 0 * mm, "dz" : -99.06 * mm, "makeCopy" : true});
        }
        {
            var Q0;
            Q0=makeQuery(id+"F9.opPattern","COPY",BODY,{"derivedFrom":makeQuery(id+"F8.opPattern","COPY",BODY,{"derivedFrom":makeQuery(id+"F7.opPattern","COPY",BODY,{"derivedFrom":makeQuery(id+"F1.opExtrude","SWEPT_BODY",BODY,{"disambiguationData":[OSD([sQuery(id+"F0.wireOp",EDGE,"E0.right"),sQuery(id+"F0.wireOp",EDGE,"E1"),sQuery(id+"F0.wireOp",EDGE,"E2"),sQuery(id+"F0.wireOp",EDGE,"E3"),sQuery(id+"F0.wireOp",EDGE,"E4"),sQuery(id+"F0.wireOp",EDGE,"E5"),sQuery(id+"F0.wireOp",EDGE,"E6.filletArc"),sQuery(id+"F0.wireOp",EDGE,"E7.filletArc"),sQuery(id+"F0.wireOp",EDGE,"E8.filletArc"),sQuery(id+"F0.wireOp",EDGE,"E9.filletArc"),sQuery(id+"F0.wireOp",EDGE,"E10.filletArc"),sQuery(id+"F0.wireOp",EDGE,"E11"),sQuery(id+"F0.wireOp",EDGE,"E17.filletArc"),sQuery(id+"F0.wireOp",EDGE,"E18.left"),sQuery(id+"F0.wireOp",EDGE,"E12"),sQuery(id+"F0.wireOp",EDGE,"E19"),sQuery(id+"F0.wireOp",EDGE,"E21.filletArc"),sQuery(id+"F0.wireOp",EDGE,"E22.filletArc"),sQuery(id+"F0.wireOp",EDGE,"E23"),sQuery(id+"F0.wireOp",EDGE,"E24.filletArc"),sQuery(id+"F0.wireOp",EDGE,"E25"),sQuery(id+"F0.wireOp",EDGE,"E26"),sQuery(id+"F0.wireOp",EDGE,"E27"),sQuery(id+"F0.wireOp",EDGE,"E28"),sQuery(id+"F0.wireOp",EDGE,"E29"),sQuery(id+"F0.wireOp",EDGE,"E30"),sQuery(id+"F0.wireOp",EDGE,"E31"),sQuery(id+"F0.wireOp",EDGE,"E32"),sQuery(id+"F0.wireOp",EDGE,"E33"),sQuery(id+"F0.wireOp",EDGE,"E34"),sQuery(id+"F0.wireOp",EDGE,"E35"),sQuery(id+"F0.wireOp",EDGE,"E36"),sQuery(id+"F0.wireOp",EDGE,"E37"),sQuery(id+"F0.wireOp",EDGE,"E38"),sQuery(id+"F0.wireOp",EDGE,"E39"),sQuery(id+"F0.wireOp",EDGE,"E40"),sQuery(id+"F0.wireOp",EDGE,"E41"),sQuery(id+"F0.wireOp",EDGE,"E42"),sQuery(id+"F0.wireOp",EDGE,"E43"),sQuery(id+"F0.wireOp",EDGE,"E44"),sQuery(id+"F0.wireOp",EDGE,"E45"),sQuery(id+"F0.wireOp",EDGE,"E46"),sQuery(id+"F0.wireOp",EDGE,"E47"),sQuery(id+"F0.wireOp",EDGE,"E48"),sQuery(id+"F0.wireOp",EDGE,"E49"),sQuery(id+"F0.wireOp",EDGE,"E50"),sQuery(id+"F0.wireOp",EDGE,"E51"),sQuery(id+"F0.wireOp",EDGE,"E52"),sQuery(id+"F0.wireOp",EDGE,"E53"),sQuery(id+"F0.wireOp",EDGE,"E54"),sQuery(id+"F0.wireOp",EDGE,"E55"),sQuery(id+"F0.wireOp",EDGE,"E56"),sQuery(id+"F0.wireOp",EDGE,"E57"),sQuery(id+"F0.wireOp",EDGE,"E59"),sQuery(id+"F0.wireOp",EDGE,"E61"),sQuery(id+"F0.wireOp",EDGE,"E62"),sQuery(id+"F0.wireOp",EDGE,"E63"),sQuery(id+"F0.wireOp",EDGE,"E64"),sQuery(id+"F0.wireOp",EDGE,"E65"),sQuery(id+"F0.wireOp",EDGE,"E66"),sQuery(id+"F0.wireOp",EDGE,"E67"),sQuery(id+"F0.wireOp",EDGE,"E68"),sQuery(id+"F0.wireOp",EDGE,"E69"),sQuery(id+"F0.wireOp",EDGE,"E70"),sQuery(id+"F0.wireOp",EDGE,"E71"),sQuery(id+"F0.wireOp",EDGE,"E72"),sQuery(id+"F0.wireOp",EDGE,"E73"),sQuery(id+"F0.wireOp",EDGE,"E74"),sQuery(id+"F0.wireOp",EDGE,"E75"),sQuery(id+"F0.wireOp",EDGE,"E76"),sQuery(id+"F0.wireOp",EDGE,"E77"),sQuery(id+"F0.wireOp",EDGE,"E78"),sQuery(id+"F0.wireOp",EDGE,"E79"),sQuery(id+"F0.wireOp",EDGE,"E80"),sQuery(id+"F0.wireOp",EDGE,"E81"),sQuery(id+"F0.wireOp",EDGE,"E82"),sQuery(id+"F0.wireOp",EDGE,"E83"),sQuery(id+"F0.wireOp",EDGE,"E84"),sQuery(id+"F0.wireOp",EDGE,"E85"),sQuery(id+"F0.wireOp",EDGE,"E86"),sQuery(id+"F0.wireOp",EDGE,"E87"),sQuery(id+"F0.wireOp",EDGE,"E88"),sQuery(id+"F0.wireOp",EDGE,"E89"),sQuery(id+"F0.wireOp",EDGE,"E90"),sQuery(id+"F0.wireOp",EDGE,"E91"),sQuery(id+"F0.wireOp",EDGE,"E92"),sQuery(id+"F0.wireOp",EDGE,"E93"),sQuery(id+"F0.wireOp",EDGE,"E94"),sQuery(id+"F0.wireOp",EDGE,"E96"),sQuery(id+"F0.wireOp",EDGE,"E99")])]}),"instanceName":"1"}),"instanceName":"1"}),"instanceName":"1"});
            transform(context, id + "F10", {"entities" : qUnion([Q0]), "transformType" : TransformType.TRANSLATION_3D, "dx" : 0 * mm, "dy" : 0 * mm, "dz" : -99.06 * mm, "makeCopy" : true});
        }
        {
            var Q0;
            Q0=makeQuery(id+"F10.opPattern","COPY",BODY,{"derivedFrom":makeQuery(id+"F9.opPattern","COPY",BODY,{"derivedFrom":makeQuery(id+"F8.opPattern","COPY",BODY,{"derivedFrom":makeQuery(id+"F7.opPattern","COPY",BODY,{"derivedFrom":makeQuery(id+"F1.opExtrude","SWEPT_BODY",BODY,{"disambiguationData":[OSD([sQuery(id+"F0.wireOp",EDGE,"E0.right"),sQuery(id+"F0.wireOp",EDGE,"E1"),sQuery(id+"F0.wireOp",EDGE,"E2"),sQuery(id+"F0.wireOp",EDGE,"E3"),sQuery(id+"F0.wireOp",EDGE,"E4"),sQuery(id+"F0.wireOp",EDGE,"E5"),sQuery(id+"F0.wireOp",EDGE,"E6.filletArc"),sQuery(id+"F0.wireOp",EDGE,"E7.filletArc"),sQuery(id+"F0.wireOp",EDGE,"E8.filletArc"),sQuery(id+"F0.wireOp",EDGE,"E9.filletArc"),sQuery(id+"F0.wireOp",EDGE,"E10.filletArc"),sQuery(id+"F0.wireOp",EDGE,"E11"),sQuery(id+"F0.wireOp",EDGE,"E17.filletArc"),sQuery(id+"F0.wireOp",EDGE,"E18.left"),sQuery(id+"F0.wireOp",EDGE,"E12"),sQuery(id+"F0.wireOp",EDGE,"E19"),sQuery(id+"F0.wireOp",EDGE,"E21.filletArc"),sQuery(id+"F0.wireOp",EDGE,"E22.filletArc"),sQuery(id+"F0.wireOp",EDGE,"E23"),sQuery(id+"F0.wireOp",EDGE,"E24.filletArc"),sQuery(id+"F0.wireOp",EDGE,"E25"),sQuery(id+"F0.wireOp",EDGE,"E26"),sQuery(id+"F0.wireOp",EDGE,"E27"),sQuery(id+"F0.wireOp",EDGE,"E28"),sQuery(id+"F0.wireOp",EDGE,"E29"),sQuery(id+"F0.wireOp",EDGE,"E30"),sQuery(id+"F0.wireOp",EDGE,"E31"),sQuery(id+"F0.wireOp",EDGE,"E32"),sQuery(id+"F0.wireOp",EDGE,"E33"),sQuery(id+"F0.wireOp",EDGE,"E34"),sQuery(id+"F0.wireOp",EDGE,"E35"),sQuery(id+"F0.wireOp",EDGE,"E36"),sQuery(id+"F0.wireOp",EDGE,"E37"),sQuery(id+"F0.wireOp",EDGE,"E38"),sQuery(id+"F0.wireOp",EDGE,"E39"),sQuery(id+"F0.wireOp",EDGE,"E40"),sQuery(id+"F0.wireOp",EDGE,"E41"),sQuery(id+"F0.wireOp",EDGE,"E42"),sQuery(id+"F0.wireOp",EDGE,"E43"),sQuery(id+"F0.wireOp",EDGE,"E44"),sQuery(id+"F0.wireOp",EDGE,"E45"),sQuery(id+"F0.wireOp",EDGE,"E46"),sQuery(id+"F0.wireOp",EDGE,"E47"),sQuery(id+"F0.wireOp",EDGE,"E48"),sQuery(id+"F0.wireOp",EDGE,"E49"),sQuery(id+"F0.wireOp",EDGE,"E50"),sQuery(id+"F0.wireOp",EDGE,"E51"),sQuery(id+"F0.wireOp",EDGE,"E52"),sQuery(id+"F0.wireOp",EDGE,"E53"),sQuery(id+"F0.wireOp",EDGE,"E54"),sQuery(id+"F0.wireOp",EDGE,"E55"),sQuery(id+"F0.wireOp",EDGE,"E56"),sQuery(id+"F0.wireOp",EDGE,"E57"),sQuery(id+"F0.wireOp",EDGE,"E59"),sQuery(id+"F0.wireOp",EDGE,"E61"),sQuery(id+"F0.wireOp",EDGE,"E62"),sQuery(id+"F0.wireOp",EDGE,"E63"),sQuery(id+"F0.wireOp",EDGE,"E64"),sQuery(id+"F0.wireOp",EDGE,"E65"),sQuery(id+"F0.wireOp",EDGE,"E66"),sQuery(id+"F0.wireOp",EDGE,"E67"),sQuery(id+"F0.wireOp",EDGE,"E68"),sQuery(id+"F0.wireOp",EDGE,"E69"),sQuery(id+"F0.wireOp",EDGE,"E70"),sQuery(id+"F0.wireOp",EDGE,"E71"),sQuery(id+"F0.wireOp",EDGE,"E72"),sQuery(id+"F0.wireOp",EDGE,"E73"),sQuery(id+"F0.wireOp",EDGE,"E74"),sQuery(id+"F0.wireOp",EDGE,"E75"),sQuery(id+"F0.wireOp",EDGE,"E76"),sQuery(id+"F0.wireOp",EDGE,"E77"),sQuery(id+"F0.wireOp",EDGE,"E78"),sQuery(id+"F0.wireOp",EDGE,"E79"),sQuery(id+"F0.wireOp",EDGE,"E80"),sQuery(id+"F0.wireOp",EDGE,"E81"),sQuery(id+"F0.wireOp",EDGE,"E82"),sQuery(id+"F0.wireOp",EDGE,"E83"),sQuery(id+"F0.wireOp",EDGE,"E84"),sQuery(id+"F0.wireOp",EDGE,"E85"),sQuery(id+"F0.wireOp",EDGE,"E86"),sQuery(id+"F0.wireOp",EDGE,"E87"),sQuery(id+"F0.wireOp",EDGE,"E88"),sQuery(id+"F0.wireOp",EDGE,"E89"),sQuery(id+"F0.wireOp",EDGE,"E90"),sQuery(id+"F0.wireOp",EDGE,"E91"),sQuery(id+"F0.wireOp",EDGE,"E92"),sQuery(id+"F0.wireOp",EDGE,"E93"),sQuery(id+"F0.wireOp",EDGE,"E94"),sQuery(id+"F0.wireOp",EDGE,"E96"),sQuery(id+"F0.wireOp",EDGE,"E99")])]}),"instanceName":"1"}),"instanceName":"1"}),"instanceName":"1"}),"instanceName":"1"});
            transform(context, id + "F11", {"entities" : qUnion([Q0]), "transformType" : TransformType.TRANSLATION_3D, "dx" : 130.8 * mm, "dy" : 0 * mm, "dz" : 390.53 * mm, "makeCopy" : true});
        }
        {
            var Q0;
            Q0=makeQuery(id+"F11.opPattern","COPY",BODY,{"derivedFrom":makeQuery(id+"F10.opPattern","COPY",BODY,{"derivedFrom":makeQuery(id+"F9.opPattern","COPY",BODY,{"derivedFrom":makeQuery(id+"F8.opPattern","COPY",BODY,{"derivedFrom":makeQuery(id+"F7.opPattern","COPY",BODY,{"derivedFrom":makeQuery(id+"F1.opExtrude","SWEPT_BODY",BODY,{"disambiguationData":[OSD([sQuery(id+"F0.wireOp",EDGE,"E0.right"),sQuery(id+"F0.wireOp",EDGE,"E1"),sQuery(id+"F0.wireOp",EDGE,"E2"),sQuery(id+"F0.wireOp",EDGE,"E3"),sQuery(id+"F0.wireOp",EDGE,"E4"),sQuery(id+"F0.wireOp",EDGE,"E5"),sQuery(id+"F0.wireOp",EDGE,"E6.filletArc"),sQuery(id+"F0.wireOp",EDGE,"E7.filletArc"),sQuery(id+"F0.wireOp",EDGE,"E8.filletArc"),sQuery(id+"F0.wireOp",EDGE,"E9.filletArc"),sQuery(id+"F0.wireOp",EDGE,"E10.filletArc"),sQuery(id+"F0.wireOp",EDGE,"E11"),sQuery(id+"F0.wireOp",EDGE,"E17.filletArc"),sQuery(id+"F0.wireOp",EDGE,"E18.left"),sQuery(id+"F0.wireOp",EDGE,"E12"),sQuery(id+"F0.wireOp",EDGE,"E19"),sQuery(id+"F0.wireOp",EDGE,"E21.filletArc"),sQuery(id+"F0.wireOp",EDGE,"E22.filletArc"),sQuery(id+"F0.wireOp",EDGE,"E23"),sQuery(id+"F0.wireOp",EDGE,"E24.filletArc"),sQuery(id+"F0.wireOp",EDGE,"E25"),sQuery(id+"F0.wireOp",EDGE,"E26"),sQuery(id+"F0.wireOp",EDGE,"E27"),sQuery(id+"F0.wireOp",EDGE,"E28"),sQuery(id+"F0.wireOp",EDGE,"E29"),sQuery(id+"F0.wireOp",EDGE,"E30"),sQuery(id+"F0.wireOp",EDGE,"E31"),sQuery(id+"F0.wireOp",EDGE,"E32"),sQuery(id+"F0.wireOp",EDGE,"E33"),sQuery(id+"F0.wireOp",EDGE,"E34"),sQuery(id+"F0.wireOp",EDGE,"E35"),sQuery(id+"F0.wireOp",EDGE,"E36"),sQuery(id+"F0.wireOp",EDGE,"E37"),sQuery(id+"F0.wireOp",EDGE,"E38"),sQuery(id+"F0.wireOp",EDGE,"E39"),sQuery(id+"F0.wireOp",EDGE,"E40"),sQuery(id+"F0.wireOp",EDGE,"E41"),sQuery(id+"F0.wireOp",EDGE,"E42"),sQuery(id+"F0.wireOp",EDGE,"E43"),sQuery(id+"F0.wireOp",EDGE,"E44"),sQuery(id+"F0.wireOp",EDGE,"E45"),sQuery(id+"F0.wireOp",EDGE,"E46"),sQuery(id+"F0.wireOp",EDGE,"E47"),sQuery(id+"F0.wireOp",EDGE,"E48"),sQuery(id+"F0.wireOp",EDGE,"E49"),sQuery(id+"F0.wireOp",EDGE,"E50"),sQuery(id+"F0.wireOp",EDGE,"E51"),sQuery(id+"F0.wireOp",EDGE,"E52"),sQuery(id+"F0.wireOp",EDGE,"E53"),sQuery(id+"F0.wireOp",EDGE,"E54"),sQuery(id+"F0.wireOp",EDGE,"E55"),sQuery(id+"F0.wireOp",EDGE,"E56"),sQuery(id+"F0.wireOp",EDGE,"E57"),sQuery(id+"F0.wireOp",EDGE,"E59"),sQuery(id+"F0.wireOp",EDGE,"E61"),sQuery(id+"F0.wireOp",EDGE,"E62"),sQuery(id+"F0.wireOp",EDGE,"E63"),sQuery(id+"F0.wireOp",EDGE,"E64"),sQuery(id+"F0.wireOp",EDGE,"E65"),sQuery(id+"F0.wireOp",EDGE,"E66"),sQuery(id+"F0.wireOp",EDGE,"E67"),sQuery(id+"F0.wireOp",EDGE,"E68"),sQuery(id+"F0.wireOp",EDGE,"E69"),sQuery(id+"F0.wireOp",EDGE,"E70"),sQuery(id+"F0.wireOp",EDGE,"E71"),sQuery(id+"F0.wireOp",EDGE,"E72"),sQuery(id+"F0.wireOp",EDGE,"E73"),sQuery(id+"F0.wireOp",EDGE,"E74"),sQuery(id+"F0.wireOp",EDGE,"E75"),sQuery(id+"F0.wireOp",EDGE,"E76"),sQuery(id+"F0.wireOp",EDGE,"E77"),sQuery(id+"F0.wireOp",EDGE,"E78"),sQuery(id+"F0.wireOp",EDGE,"E79"),sQuery(id+"F0.wireOp",EDGE,"E80"),sQuery(id+"F0.wireOp",EDGE,"E81"),sQuery(id+"F0.wireOp",EDGE,"E82"),sQuery(id+"F0.wireOp",EDGE,"E83"),sQuery(id+"F0.wireOp",EDGE,"E84"),sQuery(id+"F0.wireOp",EDGE,"E85"),sQuery(id+"F0.wireOp",EDGE,"E86"),sQuery(id+"F0.wireOp",EDGE,"E87"),sQuery(id+"F0.wireOp",EDGE,"E88"),sQuery(id+"F0.wireOp",EDGE,"E89"),sQuery(id+"F0.wireOp",EDGE,"E90"),sQuery(id+"F0.wireOp",EDGE,"E91"),sQuery(id+"F0.wireOp",EDGE,"E92"),sQuery(id+"F0.wireOp",EDGE,"E93"),sQuery(id+"F0.wireOp",EDGE,"E94"),sQuery(id+"F0.wireOp",EDGE,"E96"),sQuery(id+"F0.wireOp",EDGE,"E99")])]}),"instanceName":"1"}),"instanceName":"1"}),"instanceName":"1"}),"instanceName":"1"}),"instanceName":"1"});
            transform(context, id + "F12", {"entities" : qUnion([Q0]), "transformType" : TransformType.TRANSLATION_3D, "dx" : 0 * mm, "dy" : 0 * mm, "dz" : -99.06 * mm, "makeCopy" : true});
        }
        {
            var Q0;
            Q0=makeQuery(id+"F12.opPattern","COPY",BODY,{"derivedFrom":makeQuery(id+"F11.opPattern","COPY",BODY,{"derivedFrom":makeQuery(id+"F10.opPattern","COPY",BODY,{"derivedFrom":makeQuery(id+"F9.opPattern","COPY",BODY,{"derivedFrom":makeQuery(id+"F8.opPattern","COPY",BODY,{"derivedFrom":makeQuery(id+"F7.opPattern","COPY",BODY,{"derivedFrom":makeQuery(id+"F1.opExtrude","SWEPT_BODY",BODY,{"disambiguationData":[OSD([sQuery(id+"F0.wireOp",EDGE,"E0.right"),sQuery(id+"F0.wireOp",EDGE,"E1"),sQuery(id+"F0.wireOp",EDGE,"E2"),sQuery(id+"F0.wireOp",EDGE,"E3"),sQuery(id+"F0.wireOp",EDGE,"E4"),sQuery(id+"F0.wireOp",EDGE,"E5"),sQuery(id+"F0.wireOp",EDGE,"E6.filletArc"),sQuery(id+"F0.wireOp",EDGE,"E7.filletArc"),sQuery(id+"F0.wireOp",EDGE,"E8.filletArc"),sQuery(id+"F0.wireOp",EDGE,"E9.filletArc"),sQuery(id+"F0.wireOp",EDGE,"E10.filletArc"),sQuery(id+"F0.wireOp",EDGE,"E11"),sQuery(id+"F0.wireOp",EDGE,"E17.filletArc"),sQuery(id+"F0.wireOp",EDGE,"E18.left"),sQuery(id+"F0.wireOp",EDGE,"E12"),sQuery(id+"F0.wireOp",EDGE,"E19"),sQuery(id+"F0.wireOp",EDGE,"E21.filletArc"),sQuery(id+"F0.wireOp",EDGE,"E22.filletArc"),sQuery(id+"F0.wireOp",EDGE,"E23"),sQuery(id+"F0.wireOp",EDGE,"E24.filletArc"),sQuery(id+"F0.wireOp",EDGE,"E25"),sQuery(id+"F0.wireOp",EDGE,"E26"),sQuery(id+"F0.wireOp",EDGE,"E27"),sQuery(id+"F0.wireOp",EDGE,"E28"),sQuery(id+"F0.wireOp",EDGE,"E29"),sQuery(id+"F0.wireOp",EDGE,"E30"),sQuery(id+"F0.wireOp",EDGE,"E31"),sQuery(id+"F0.wireOp",EDGE,"E32"),sQuery(id+"F0.wireOp",EDGE,"E33"),sQuery(id+"F0.wireOp",EDGE,"E34"),sQuery(id+"F0.wireOp",EDGE,"E35"),sQuery(id+"F0.wireOp",EDGE,"E36"),sQuery(id+"F0.wireOp",EDGE,"E37"),sQuery(id+"F0.wireOp",EDGE,"E38"),sQuery(id+"F0.wireOp",EDGE,"E39"),sQuery(id+"F0.wireOp",EDGE,"E40"),sQuery(id+"F0.wireOp",EDGE,"E41"),sQuery(id+"F0.wireOp",EDGE,"E42"),sQuery(id+"F0.wireOp",EDGE,"E43"),sQuery(id+"F0.wireOp",EDGE,"E44"),sQuery(id+"F0.wireOp",EDGE,"E45"),sQuery(id+"F0.wireOp",EDGE,"E46"),sQuery(id+"F0.wireOp",EDGE,"E47"),sQuery(id+"F0.wireOp",EDGE,"E48"),sQuery(id+"F0.wireOp",EDGE,"E49"),sQuery(id+"F0.wireOp",EDGE,"E50"),sQuery(id+"F0.wireOp",EDGE,"E51"),sQuery(id+"F0.wireOp",EDGE,"E52"),sQuery(id+"F0.wireOp",EDGE,"E53"),sQuery(id+"F0.wireOp",EDGE,"E54"),sQuery(id+"F0.wireOp",EDGE,"E55"),sQuery(id+"F0.wireOp",EDGE,"E56"),sQuery(id+"F0.wireOp",EDGE,"E57"),sQuery(id+"F0.wireOp",EDGE,"E59"),sQuery(id+"F0.wireOp",EDGE,"E61"),sQuery(id+"F0.wireOp",EDGE,"E62"),sQuery(id+"F0.wireOp",EDGE,"E63"),sQuery(id+"F0.wireOp",EDGE,"E64"),sQuery(id+"F0.wireOp",EDGE,"E65"),sQuery(id+"F0.wireOp",EDGE,"E66"),sQuery(id+"F0.wireOp",EDGE,"E67"),sQuery(id+"F0.wireOp",EDGE,"E68"),sQuery(id+"F0.wireOp",EDGE,"E69"),sQuery(id+"F0.wireOp",EDGE,"E70"),sQuery(id+"F0.wireOp",EDGE,"E71"),sQuery(id+"F0.wireOp",EDGE,"E72"),sQuery(id+"F0.wireOp",EDGE,"E73"),sQuery(id+"F0.wireOp",EDGE,"E74"),sQuery(id+"F0.wireOp",EDGE,"E75"),sQuery(id+"F0.wireOp",EDGE,"E76"),sQuery(id+"F0.wireOp",EDGE,"E77"),sQuery(id+"F0.wireOp",EDGE,"E78"),sQuery(id+"F0.wireOp",EDGE,"E79"),sQuery(id+"F0.wireOp",EDGE,"E80"),sQuery(id+"F0.wireOp",EDGE,"E81"),sQuery(id+"F0.wireOp",EDGE,"E82"),sQuery(id+"F0.wireOp",EDGE,"E83"),sQuery(id+"F0.wireOp",EDGE,"E84"),sQuery(id+"F0.wireOp",EDGE,"E85"),sQuery(id+"F0.wireOp",EDGE,"E86"),sQuery(id+"F0.wireOp",EDGE,"E87"),sQuery(id+"F0.wireOp",EDGE,"E88"),sQuery(id+"F0.wireOp",EDGE,"E89"),sQuery(id+"F0.wireOp",EDGE,"E90"),sQuery(id+"F0.wireOp",EDGE,"E91"),sQuery(id+"F0.wireOp",EDGE,"E92"),sQuery(id+"F0.wireOp",EDGE,"E93"),sQuery(id+"F0.wireOp",EDGE,"E94"),sQuery(id+"F0.wireOp",EDGE,"E96"),sQuery(id+"F0.wireOp",EDGE,"E99")])]}),"instanceName":"1"}),"instanceName":"1"}),"instanceName":"1"}),"instanceName":"1"}),"instanceName":"1"}),"instanceName":"1"});
            transform(context, id + "F13", {"entities" : qUnion([Q0]), "transformType" : TransformType.TRANSLATION_3D, "dx" : 0 * mm, "dy" : 0 * mm, "dz" : -99.06 * mm, "makeCopy" : true});
        }
        {
            var Q0;
            Q0=makeQuery(id+"F13.opPattern","COPY",BODY,{"derivedFrom":makeQuery(id+"F12.opPattern","COPY",BODY,{"derivedFrom":makeQuery(id+"F11.opPattern","COPY",BODY,{"derivedFrom":makeQuery(id+"F10.opPattern","COPY",BODY,{"derivedFrom":makeQuery(id+"F9.opPattern","COPY",BODY,{"derivedFrom":makeQuery(id+"F8.opPattern","COPY",BODY,{"derivedFrom":makeQuery(id+"F7.opPattern","COPY",BODY,{"derivedFrom":makeQuery(id+"F1.opExtrude","SWEPT_BODY",BODY,{"disambiguationData":[OSD([sQuery(id+"F0.wireOp",EDGE,"E0.right"),sQuery(id+"F0.wireOp",EDGE,"E1"),sQuery(id+"F0.wireOp",EDGE,"E2"),sQuery(id+"F0.wireOp",EDGE,"E3"),sQuery(id+"F0.wireOp",EDGE,"E4"),sQuery(id+"F0.wireOp",EDGE,"E5"),sQuery(id+"F0.wireOp",EDGE,"E6.filletArc"),sQuery(id+"F0.wireOp",EDGE,"E7.filletArc"),sQuery(id+"F0.wireOp",EDGE,"E8.filletArc"),sQuery(id+"F0.wireOp",EDGE,"E9.filletArc"),sQuery(id+"F0.wireOp",EDGE,"E10.filletArc"),sQuery(id+"F0.wireOp",EDGE,"E11"),sQuery(id+"F0.wireOp",EDGE,"E17.filletArc"),sQuery(id+"F0.wireOp",EDGE,"E18.left"),sQuery(id+"F0.wireOp",EDGE,"E12"),sQuery(id+"F0.wireOp",EDGE,"E19"),sQuery(id+"F0.wireOp",EDGE,"E21.filletArc"),sQuery(id+"F0.wireOp",EDGE,"E22.filletArc"),sQuery(id+"F0.wireOp",EDGE,"E23"),sQuery(id+"F0.wireOp",EDGE,"E24.filletArc"),sQuery(id+"F0.wireOp",EDGE,"E25"),sQuery(id+"F0.wireOp",EDGE,"E26"),sQuery(id+"F0.wireOp",EDGE,"E27"),sQuery(id+"F0.wireOp",EDGE,"E28"),sQuery(id+"F0.wireOp",EDGE,"E29"),sQuery(id+"F0.wireOp",EDGE,"E30"),sQuery(id+"F0.wireOp",EDGE,"E31"),sQuery(id+"F0.wireOp",EDGE,"E32"),sQuery(id+"F0.wireOp",EDGE,"E33"),sQuery(id+"F0.wireOp",EDGE,"E34"),sQuery(id+"F0.wireOp",EDGE,"E35"),sQuery(id+"F0.wireOp",EDGE,"E36"),sQuery(id+"F0.wireOp",EDGE,"E37"),sQuery(id+"F0.wireOp",EDGE,"E38"),sQuery(id+"F0.wireOp",EDGE,"E39"),sQuery(id+"F0.wireOp",EDGE,"E40"),sQuery(id+"F0.wireOp",EDGE,"E41"),sQuery(id+"F0.wireOp",EDGE,"E42"),sQuery(id+"F0.wireOp",EDGE,"E43"),sQuery(id+"F0.wireOp",EDGE,"E44"),sQuery(id+"F0.wireOp",EDGE,"E45"),sQuery(id+"F0.wireOp",EDGE,"E46"),sQuery(id+"F0.wireOp",EDGE,"E47"),sQuery(id+"F0.wireOp",EDGE,"E48"),sQuery(id+"F0.wireOp",EDGE,"E49"),sQuery(id+"F0.wireOp",EDGE,"E50"),sQuery(id+"F0.wireOp",EDGE,"E51"),sQuery(id+"F0.wireOp",EDGE,"E52"),sQuery(id+"F0.wireOp",EDGE,"E53"),sQuery(id+"F0.wireOp",EDGE,"E54"),sQuery(id+"F0.wireOp",EDGE,"E55"),sQuery(id+"F0.wireOp",EDGE,"E56"),sQuery(id+"F0.wireOp",EDGE,"E57"),sQuery(id+"F0.wireOp",EDGE,"E59"),sQuery(id+"F0.wireOp",EDGE,"E61"),sQuery(id+"F0.wireOp",EDGE,"E62"),sQuery(id+"F0.wireOp",EDGE,"E63"),sQuery(id+"F0.wireOp",EDGE,"E64"),sQuery(id+"F0.wireOp",EDGE,"E65"),sQuery(id+"F0.wireOp",EDGE,"E66"),sQuery(id+"F0.wireOp",EDGE,"E67"),sQuery(id+"F0.wireOp",EDGE,"E68"),sQuery(id+"F0.wireOp",EDGE,"E69"),sQuery(id+"F0.wireOp",EDGE,"E70"),sQuery(id+"F0.wireOp",EDGE,"E71"),sQuery(id+"F0.wireOp",EDGE,"E72"),sQuery(id+"F0.wireOp",EDGE,"E73"),sQuery(id+"F0.wireOp",EDGE,"E74"),sQuery(id+"F0.wireOp",EDGE,"E75"),sQuery(id+"F0.wireOp",EDGE,"E76"),sQuery(id+"F0.wireOp",EDGE,"E77"),sQuery(id+"F0.wireOp",EDGE,"E78"),sQuery(id+"F0.wireOp",EDGE,"E79"),sQuery(id+"F0.wireOp",EDGE,"E80"),sQuery(id+"F0.wireOp",EDGE,"E81"),sQuery(id+"F0.wireOp",EDGE,"E82"),sQuery(id+"F0.wireOp",EDGE,"E83"),sQuery(id+"F0.wireOp",EDGE,"E84"),sQuery(id+"F0.wireOp",EDGE,"E85"),sQuery(id+"F0.wireOp",EDGE,"E86"),sQuery(id+"F0.wireOp",EDGE,"E87"),sQuery(id+"F0.wireOp",EDGE,"E88"),sQuery(id+"F0.wireOp",EDGE,"E89"),sQuery(id+"F0.wireOp",EDGE,"E90"),sQuery(id+"F0.wireOp",EDGE,"E91"),sQuery(id+"F0.wireOp",EDGE,"E92"),sQuery(id+"F0.wireOp",EDGE,"E93"),sQuery(id+"F0.wireOp",EDGE,"E94"),sQuery(id+"F0.wireOp",EDGE,"E96"),sQuery(id+"F0.wireOp",EDGE,"E99")])]}),"instanceName":"1"}),"instanceName":"1"}),"instanceName":"1"}),"instanceName":"1"}),"instanceName":"1"}),"instanceName":"1"}),"instanceName":"1"});
            transform(context, id + "F14", {"entities" : qUnion([Q0]), "transformType" : TransformType.TRANSLATION_3D, "dx" : 0 * mm, "dy" : 0 * mm, "dz" : -99.06 * mm, "makeCopy" : true});
        }
        {
            var Q0;
            Q0=makeQuery(id+"F10.opPattern","COPY",BODY,{"derivedFrom":makeQuery(id+"F9.opPattern","COPY",BODY,{"derivedFrom":makeQuery(id+"F8.opPattern","COPY",BODY,{"derivedFrom":makeQuery(id+"F7.opPattern","COPY",BODY,{"derivedFrom":makeQuery(id+"F1.opExtrude","SWEPT_BODY",BODY,{"disambiguationData":[OSD([sQuery(id+"F0.wireOp",EDGE,"E0.right"),sQuery(id+"F0.wireOp",EDGE,"E1"),sQuery(id+"F0.wireOp",EDGE,"E2"),sQuery(id+"F0.wireOp",EDGE,"E3"),sQuery(id+"F0.wireOp",EDGE,"E4"),sQuery(id+"F0.wireOp",EDGE,"E5"),sQuery(id+"F0.wireOp",EDGE,"E6.filletArc"),sQuery(id+"F0.wireOp",EDGE,"E7.filletArc"),sQuery(id+"F0.wireOp",EDGE,"E8.filletArc"),sQuery(id+"F0.wireOp",EDGE,"E9.filletArc"),sQuery(id+"F0.wireOp",EDGE,"E10.filletArc"),sQuery(id+"F0.wireOp",EDGE,"E11"),sQuery(id+"F0.wireOp",EDGE,"E17.filletArc"),sQuery(id+"F0.wireOp",EDGE,"E18.left"),sQuery(id+"F0.wireOp",EDGE,"E12"),sQuery(id+"F0.wireOp",EDGE,"E19"),sQuery(id+"F0.wireOp",EDGE,"E21.filletArc"),sQuery(id+"F0.wireOp",EDGE,"E22.filletArc"),sQuery(id+"F0.wireOp",EDGE,"E23"),sQuery(id+"F0.wireOp",EDGE,"E24.filletArc"),sQuery(id+"F0.wireOp",EDGE,"E25"),sQuery(id+"F0.wireOp",EDGE,"E26"),sQuery(id+"F0.wireOp",EDGE,"E27"),sQuery(id+"F0.wireOp",EDGE,"E28"),sQuery(id+"F0.wireOp",EDGE,"E29"),sQuery(id+"F0.wireOp",EDGE,"E30"),sQuery(id+"F0.wireOp",EDGE,"E31"),sQuery(id+"F0.wireOp",EDGE,"E32"),sQuery(id+"F0.wireOp",EDGE,"E33"),sQuery(id+"F0.wireOp",EDGE,"E34"),sQuery(id+"F0.wireOp",EDGE,"E35"),sQuery(id+"F0.wireOp",EDGE,"E36"),sQuery(id+"F0.wireOp",EDGE,"E37"),sQuery(id+"F0.wireOp",EDGE,"E38"),sQuery(id+"F0.wireOp",EDGE,"E39"),sQuery(id+"F0.wireOp",EDGE,"E40"),sQuery(id+"F0.wireOp",EDGE,"E41"),sQuery(id+"F0.wireOp",EDGE,"E42"),sQuery(id+"F0.wireOp",EDGE,"E43"),sQuery(id+"F0.wireOp",EDGE,"E44"),sQuery(id+"F0.wireOp",EDGE,"E45"),sQuery(id+"F0.wireOp",EDGE,"E46"),sQuery(id+"F0.wireOp",EDGE,"E47"),sQuery(id+"F0.wireOp",EDGE,"E48"),sQuery(id+"F0.wireOp",EDGE,"E49"),sQuery(id+"F0.wireOp",EDGE,"E50"),sQuery(id+"F0.wireOp",EDGE,"E51"),sQuery(id+"F0.wireOp",EDGE,"E52"),sQuery(id+"F0.wireOp",EDGE,"E53"),sQuery(id+"F0.wireOp",EDGE,"E54"),sQuery(id+"F0.wireOp",EDGE,"E55"),sQuery(id+"F0.wireOp",EDGE,"E56"),sQuery(id+"F0.wireOp",EDGE,"E57"),sQuery(id+"F0.wireOp",EDGE,"E59"),sQuery(id+"F0.wireOp",EDGE,"E61"),sQuery(id+"F0.wireOp",EDGE,"E62"),sQuery(id+"F0.wireOp",EDGE,"E63"),sQuery(id+"F0.wireOp",EDGE,"E64"),sQuery(id+"F0.wireOp",EDGE,"E65"),sQuery(id+"F0.wireOp",EDGE,"E66"),sQuery(id+"F0.wireOp",EDGE,"E67"),sQuery(id+"F0.wireOp",EDGE,"E68"),sQuery(id+"F0.wireOp",EDGE,"E69"),sQuery(id+"F0.wireOp",EDGE,"E70"),sQuery(id+"F0.wireOp",EDGE,"E71"),sQuery(id+"F0.wireOp",EDGE,"E72"),sQuery(id+"F0.wireOp",EDGE,"E73"),sQuery(id+"F0.wireOp",EDGE,"E74"),sQuery(id+"F0.wireOp",EDGE,"E75"),sQuery(id+"F0.wireOp",EDGE,"E76"),sQuery(id+"F0.wireOp",EDGE,"E77"),sQuery(id+"F0.wireOp",EDGE,"E78"),sQuery(id+"F0.wireOp",EDGE,"E79"),sQuery(id+"F0.wireOp",EDGE,"E80"),sQuery(id+"F0.wireOp",EDGE,"E81"),sQuery(id+"F0.wireOp",EDGE,"E82"),sQuery(id+"F0.wireOp",EDGE,"E83"),sQuery(id+"F0.wireOp",EDGE,"E84"),sQuery(id+"F0.wireOp",EDGE,"E85"),sQuery(id+"F0.wireOp",EDGE,"E86"),sQuery(id+"F0.wireOp",EDGE,"E87"),sQuery(id+"F0.wireOp",EDGE,"E88"),sQuery(id+"F0.wireOp",EDGE,"E89"),sQuery(id+"F0.wireOp",EDGE,"E90"),sQuery(id+"F0.wireOp",EDGE,"E91"),sQuery(id+"F0.wireOp",EDGE,"E92"),sQuery(id+"F0.wireOp",EDGE,"E93"),sQuery(id+"F0.wireOp",EDGE,"E94"),sQuery(id+"F0.wireOp",EDGE,"E96"),sQuery(id+"F0.wireOp",EDGE,"E99")])]}),"instanceName":"1"}),"instanceName":"1"}),"instanceName":"1"}),"instanceName":"1"});
            transform(context, id + "F15", {"entities" : qUnion([Q0]), "transformType" : TransformType.TRANSLATION_3D, "dx" : 989.96 * mm, "dy" : 5.7 * mm, "dz" : -34.3 * mm, "makeCopy" : true});
        }
        {
            var Q0;
            Q0=qCreatedBy(makeId("Front.planeOp"),FACE);
            var sketch = newSketch(context, id + "F16", { "sketchPlane" : qUnion([Q0])});
            skArc(sketch, "E103", {"start": v(85.04, 209.64) * mm, "mid": v(30.97, 273.43) * mm, "end": v(-49.18, 297.28) * mm});
            skLineSegment(sketch, "E104", {"start": v(85.04, 196.22) * mm, "end": v(90.12, 196.22) * mm});
            skArc(sketch, "E105", {"start": v(90.12, 209.64) * mm, "mid": v(34.49, 277.06) * mm, "end": v(-49.18, 302.36) * mm});
            skLineSegment(sketch, "E106", {"start": v(-16.56, 300.27) * mm, "end": v(-11.73, 318.52) * mm});
            skLineSegment(sketch, "E107", {"start": v(-11.73, 318.52) * mm, "end": v(0.96, 315.16) * mm});
            skLineSegment(sketch, "E108", {"start": v(0.96, 315.16) * mm, "end": v(-3.87, 296.91) * mm});
            skArc(sketch, "E109", {"start": v(34.14, 279.02) * mm, "mid": v(15.79, 289.34) * mm, "end": v(-3.87, 296.91) * mm});
            skLineSegment(sketch, "E110", {"start": v(34.14, 279.02) * mm, "end": v(45.13, 294.36) * mm});
            skLineSegment(sketch, "E111", {"start": v(45.13, 294.36) * mm, "end": v(55.8, 286.72) * mm});
            skLineSegment(sketch, "E112", {"start": v(55.8, 286.72) * mm, "end": v(44.82, 271.37) * mm});
            skArc(sketch, "E113", {"start": v(74.01, 241.16) * mm, "mid": v(60.51, 257.32) * mm, "end": v(44.82, 271.37) * mm});
            skLineSegment(sketch, "E114", {"start": v(74.01, 241.16) * mm, "end": v(89.73, 251.6) * mm});
            skLineSegment(sketch, "E115", {"start": v(89.73, 251.6) * mm, "end": v(97, 240.67) * mm});
            skLineSegment(sketch, "E116", {"start": v(97, 240.67) * mm, "end": v(81.28, 230.22) * mm});
            skArc(sketch, "E117", {"start": v(91.53, 209.64) * mm, "mid": v(86.8, 220.13) * mm, "end": v(81.28, 230.22) * mm});
            skLineSegment(sketch, "E118", {"start": v(90.12, 196.22) * mm, "end": v(91.57, 196.22) * mm});
            skLineSegment(sketch, "E119", {"start": v(91.57, 196.22) * mm, "end": v(110.44, 196.22) * mm});
            skLineSegment(sketch, "E120", {"start": v(110.44, 196.22) * mm, "end": v(110.44, 209.36) * mm});
            skLineSegment(sketch, "E121", {"start": v(110.44, 209.36) * mm, "end": v(91.7, 209.36) * mm});
            skLineSegment(sketch, "E122", {"start": v(91.7, 209.36) * mm, "end": v(91.53, 209.64) * mm});
            skLineSegment(sketch, "E123", {"start": v(-28.52, 247.88) * mm, "end": v(-33.78, 229.76) * mm});
            skLineSegment(sketch, "E124", {"start": v(-33.78, 229.76) * mm, "end": v(-21.17, 226.1) * mm});
            skLineSegment(sketch, "E125", {"start": v(-21.17, 226.1) * mm, "end": v(-15.9, 244.22) * mm});
            skArc(sketch, "E126", {"start": v(10.36, 229.68) * mm, "mid": v(-2.21, 237.96) * mm, "end": v(-15.9, 244.22) * mm});
            skLineSegment(sketch, "E127", {"start": v(10.36, 229.68) * mm, "end": v(-2.2, 215.6) * mm});
            skLineSegment(sketch, "E128", {"start": v(-2.2, 215.6) * mm, "end": v(7.6, 206.86) * mm});
            skLineSegment(sketch, "E129", {"start": v(7.6, 206.86) * mm, "end": v(20.16, 220.94) * mm});
            skLineSegment(sketch, "E130", {"start": v(39.32, 196.22) * mm, "end": v(37.87, 196.22) * mm});
            skArc(sketch, "E131", {"start": v(37.87, 196.22) * mm, "mid": v(29.98, 209.27) * mm, "end": v(20.16, 220.94) * mm});
            skLineSegment(sketch, "E132", {"start": v(78.7, 196.22) * mm, "end": v(78.7, 190.94) * mm});
            skLineSegment(sketch, "E133", {"start": v(77.42, 189.67) * mm, "end": v(68.53, 189.67) * mm});
            skLineSegment(sketch, "E134", {"start": v(67.26, 190.94) * mm, "end": v(67.26, 194.95) * mm});
            skPoint(sketch, "E135.visualSharp", {"position": v(78.7, 189.67) * mm});
            skArc(sketch, "E135.filletArc", {"start": v(77.42, 189.67) * mm, "mid": v(78.32, 190.04) * mm, "end": v(78.7, 190.94) * mm});
            skPoint(sketch, "E136.visualSharp", {"position": v(67.26, 189.67) * mm});
            skArc(sketch, "E136.filletArc", {"start": v(67.26, 190.94) * mm, "mid": v(67.63, 190.04) * mm, "end": v(68.53, 189.67) * mm});
            skLineSegment(sketch, "E137", {"start": v(78.7, 196.22) * mm, "end": v(85.04, 196.22) * mm});
            skLineSegment(sketch, "E138", {"start": v(66, 196.22) * mm, "end": v(57.1, 196.22) * mm});
            skLineSegment(sketch, "E139", {"start": v(55.83, 194.95) * mm, "end": v(55.83, 189.67) * mm});
            skPoint(sketch, "E140.visualSharp", {"position": v(67.26, 196.22) * mm});
            skArc(sketch, "E140.filletArc", {"start": v(67.26, 194.95) * mm, "mid": v(66.9, 195.85) * mm, "end": v(66, 196.22) * mm});
            skPoint(sketch, "E141.visualSharp", {"position": v(55.83, 196.22) * mm});
            skArc(sketch, "E141.filletArc", {"start": v(57.1, 196.22) * mm, "mid": v(56.2, 195.85) * mm, "end": v(55.83, 194.95) * mm});
            skLineSegment(sketch, "E142", {"start": v(44.4, 189.67) * mm, "end": v(55.83, 189.67) * mm});
            skLineSegment(sketch, "E143", {"start": v(37.87, 196.22) * mm, "end": v(37.87, 189.67) * mm});
            skLineSegment(sketch, "E144", {"start": v(37.87, 189.67) * mm, "end": v(44.4, 189.67) * mm});
            skLineSegment(sketch, "E145", {"start": v(39.32, 196.22) * mm, "end": v(42.52, 189.67) * mm});
            skLineSegment(sketch, "E146", {"start": v(44.4, 196.22) * mm, "end": v(47.36, 189.67) * mm});
            skLineSegment(sketch, "E147", {"start": v(90.12, 209.64) * mm, "end": v(95.74, 196.22) * mm});
            skPoint(sketch, "E148.endSnap0", {"position": v(90.85, 196.22) * mm});
            skLineSegment(sketch, "E149", {"start": v(85.04, 209.64) * mm, "end": v(90.94, 196.22) * mm});
            skLineSegment(sketch, "E150", {"start": v(-49.18, 302.36) * mm, "end": v(-49.18, 297.28) * mm});
            skLineSegment(sketch, "E151", {"start": v(-49.18, 297.28) * mm, "end": v(-49.18, 285.85) * mm});
            skLineSegment(sketch, "E152", {"start": v(-49.18, 285.85) * mm, "end": v(-43.9, 285.85) * mm});
            skLineSegment(sketch, "E153", {"start": v(-42.63, 284.58) * mm, "end": v(-42.63, 275.69) * mm});
            skLineSegment(sketch, "E154", {"start": v(-43.9, 274.42) * mm, "end": v(-47.91, 274.42) * mm});
            skLineSegment(sketch, "E155", {"start": v(-49.18, 273.15) * mm, "end": v(-49.18, 264.26) * mm});
            skLineSegment(sketch, "E156", {"start": v(-47.91, 262.99) * mm, "end": v(-43.9, 262.99) * mm});
            skLineSegment(sketch, "E157", {"start": v(-42.63, 261.72) * mm, "end": v(-42.63, 251.34) * mm});
            skArc(sketch, "E158", {"start": v(39.32, 196.22) * mm, "mid": v(5.76, 234.8) * mm, "end": v(-42.63, 251.34) * mm});
            skArc(sketch, "E159", {"start": v(44.4, 196.22) * mm, "mid": v(9.24, 238.47) * mm, "end": v(-42.63, 256.64) * mm});
            skLineSegment(sketch, "E160", {"start": v(-16.56, 300.27) * mm, "end": v(-16.93, 298.87) * mm});
            skLineSegment(sketch, "E161", {"start": v(-28.52, 247.88) * mm, "end": v(-28.12, 249.28) * mm});
            skPoint(sketch, "E162.visualSharp", {"position": v(-42.63, 285.85) * mm});
            skArc(sketch, "E162.filletArc", {"start": v(-42.63, 284.58) * mm, "mid": v(-43, 285.47) * mm, "end": v(-43.9, 285.85) * mm});
            skPoint(sketch, "E163.visualSharp", {"position": v(-42.63, 274.42) * mm});
            skArc(sketch, "E163.filletArc", {"start": v(-43.9, 274.42) * mm, "mid": v(-43, 274.79) * mm, "end": v(-42.63, 275.69) * mm});
            skPoint(sketch, "E164.visualSharp", {"position": v(-49.18, 274.42) * mm});
            skArc(sketch, "E164.filletArc", {"start": v(-47.91, 274.42) * mm, "mid": v(-48.81, 274.04) * mm, "end": v(-49.18, 273.15) * mm});
            skPoint(sketch, "E165.visualSharp", {"position": v(-49.18, 262.99) * mm});
            skArc(sketch, "E165.filletArc", {"start": v(-49.18, 264.26) * mm, "mid": v(-48.81, 263.36) * mm, "end": v(-47.91, 262.99) * mm});
            skPoint(sketch, "E166.visualSharp", {"position": v(-42.63, 262.99) * mm});
            skArc(sketch, "E166.filletArc", {"start": v(-42.63, 261.72) * mm, "mid": v(-43, 262.61) * mm, "end": v(-43.9, 262.99) * mm});
            skSolve(sketch);
        }
        {
            var Q0;
            Q0 = qSketchRegion(id + "F16", true);
            extrude(context, id + "F17", {"entities" : qUnion([Q0]), "depth" : 3.17 * mm});
        }
        {
            var Q0;
            Q0=makeQuery(id+"F17.opExtrude","CAP_FACE",FACE,{"disambiguationData":[OSD([sQuery(id+"F16.wireOp",EDGE,"KNlQa4Zo-YTXx-w4N4-aRN1-drF1v70HGVSZ"),sQuery(id+"F16.wireOp",EDGE,"E104"),sQuery(id+"F16.wireOp",EDGE,"FqjqoJdd-gPWH-Xghq-b061-MRI81XmJMNie"),sQuery(id+"F16.wireOp",EDGE,"fIdaUP2V-rCuL-g9az-AqTW-ZxU4SovSAGXS"),sQuery(id+"F16.wireOp",EDGE,"xGjuTvcU-3kij-0HJ7-qXFS-f4At5dvGbPoV"),sQuery(id+"F16.wireOp",EDGE,"AweFUQ5t-gSvw-yYcX-pN2m-7zr78jBIP70m"),sQuery(id+"F16.wireOp",EDGE,"E106"),sQuery(id+"F16.wireOp",EDGE,"E107"),sQuery(id+"F16.wireOp",EDGE,"E108"),sQuery(id+"F16.wireOp",EDGE,"E109"),sQuery(id+"F16.wireOp",EDGE,"E110"),sQuery(id+"F16.wireOp",EDGE,"E111"),sQuery(id+"F16.wireOp",EDGE,"E112"),sQuery(id+"F16.wireOp",EDGE,"E113"),sQuery(id+"F16.wireOp",EDGE,"E114"),sQuery(id+"F16.wireOp",EDGE,"E115"),sQuery(id+"F16.wireOp",EDGE,"E116"),sQuery(id+"F16.wireOp",EDGE,"E117"),sQuery(id+"F16.wireOp",EDGE,"E118"),sQuery(id+"F16.wireOp",EDGE,"E119"),sQuery(id+"F16.wireOp",EDGE,"E120"),sQuery(id+"F16.wireOp",EDGE,"E121"),sQuery(id+"F16.wireOp",EDGE,"E122"),sQuery(id+"F16.wireOp",EDGE,"S4ZgD4fj-wu3B-b9gq-MFdI-6nMHIDOnMf1b"),sQuery(id+"F16.wireOp",EDGE,"2MMLHgPb-Od2S-jgy6-R7KS-3pFeT9BqBlrX"),sQuery(id+"F16.wireOp",EDGE,"9zRfOSmV-DnoR-IQm2-8mvr-R97rpbvwHzC0"),sQuery(id+"F16.wireOp",EDGE,"5N0TxjvZ-mL3s-Sypx-gYDa-ILURxNQzjUeC"),sQuery(id+"F16.wireOp",EDGE,"E123"),sQuery(id+"F16.wireOp",EDGE,"E124"),sQuery(id+"F16.wireOp",EDGE,"E125"),sQuery(id+"F16.wireOp",EDGE,"E126"),sQuery(id+"F16.wireOp",EDGE,"E127"),sQuery(id+"F16.wireOp",EDGE,"E128"),sQuery(id+"F16.wireOp",EDGE,"E129"),sQuery(id+"F16.wireOp",EDGE,"E131"),sQuery(id+"F16.wireOp",EDGE,"E132"),sQuery(id+"F16.wireOp",EDGE,"E133"),sQuery(id+"F16.wireOp",EDGE,"E134"),sQuery(id+"F16.wireOp",EDGE,"E135.filletArc"),sQuery(id+"F16.wireOp",EDGE,"E136.filletArc"),sQuery(id+"F16.wireOp",EDGE,"E137"),sQuery(id+"F16.wireOp",EDGE,"E138"),sQuery(id+"F16.wireOp",EDGE,"E139"),sQuery(id+"F16.wireOp",EDGE,"E140.filletArc"),sQuery(id+"F16.wireOp",EDGE,"E141.filletArc"),sQuery(id+"F16.wireOp",EDGE,"E142"),sQuery(id+"F16.wireOp",EDGE,"E143"),sQuery(id+"F16.wireOp",EDGE,"E144"),sQuery(id+"F16.wireOp",EDGE,"bTRVcH6j-3HTp-rHIk-iP38-RX5fOa6IICLK"),sQuery(id+"F16.wireOp",EDGE,"ZxG8Ixeu-TiUJ-X6Ws-LEH0-SgtDoKyzScIO"),sQuery(id+"F16.wireOp",EDGE,"iqhDDctJ-DFI0-w93G-mWSZ-jod7B4hKst5q"),sQuery(id+"F16.wireOp",EDGE,"kJg86Nbg-BVFe-9bgW-d4b1-XLPkjMBWPouF"),sQuery(id+"F16.wireOp",EDGE,"vzD8kHnG-j6Yj-tT0k-EJiF-sAF0qJC3kBsM"),sQuery(id+"F16.wireOp",EDGE,"ATLLkzoR-xLp8-PK2h-xpL1-4FHkQ0npFU1p"),sQuery(id+"F16.wireOp",EDGE,"A9BTCMLA-84TM-lB5k-Eluh-QPGjXW7soWaE"),sQuery(id+"F16.wireOp",EDGE,"R5GvcQym-SsAj-qG7A-otxq-drPFPu247RhT"),sQuery(id+"F16.wireOp",EDGE,"KW7av8gp-Ffvi-hUdM-28wj-p3RSLdVNXCTe"),sQuery(id+"F16.wireOp",EDGE,"8fdd0ad8-850c-40ae-9457-b2188aafbfc6.filletArc"),sQuery(id+"F16.wireOp",EDGE,"b7d22ab5-fd41-4537-b8d2-879762634df6.filletArc"),sQuery(id+"F16.wireOp",EDGE,"18aa52c6-2d0c-4a72-a31e-9e2052208f85.filletArc"),sQuery(id+"F16.wireOp",EDGE,"1a89a74f-9219-4d13-8580-9d6571421a05.filletArc")])],"isStart":false});
            var sketch = newSketch(context, id + "F18", { "sketchPlane" : qUnion([Q0])});
            skArc(sketch, "E167.0", {"start": v(90.12, 209.64) * mm, "mid": v(34.49, 277.06) * mm, "end": v(-49.18, 302.36) * mm});
            skArc(sketch, "E168.0", {"start": v(85.04, 209.64) * mm, "mid": v(30.97, 273.43) * mm, "end": v(-49.18, 297.28) * mm});
            skArc(sketch, "E169", {"start": v(44.4, 196.22) * mm, "mid": v(9.34, 238.57) * mm, "end": v(-42.63, 256.53) * mm});
            skArc(sketch, "E170", {"start": v(39.32, 196.22) * mm, "mid": v(6.09, 235.3) * mm, "end": v(-42.63, 251.34) * mm});
            skLineSegment(sketch, "E171", {"start": v(-42.63, 256.53) * mm, "end": v(-42.63, 251.34) * mm});
            skLineSegment(sketch, "E172", {"start": v(-49.18, 302.36) * mm, "end": v(-49.18, 297.28) * mm});
            skLineSegment(sketch, "E173", {"start": v(44.4, 196.22) * mm, "end": v(47.32, 189.67) * mm});
            skLineSegment(sketch, "E174", {"start": v(47.32, 189.67) * mm, "end": v(42.57, 189.67) * mm});
            skLineSegment(sketch, "E175", {"start": v(42.57, 189.67) * mm, "end": v(39.32, 196.22) * mm});
            skLineSegment(sketch, "E176", {"start": v(90.12, 209.64) * mm, "end": v(95.74, 196.22) * mm});
            skLineSegment(sketch, "E177", {"start": v(95.74, 196.22) * mm, "end": v(90.81, 196.22) * mm});
            skLineSegment(sketch, "E178", {"start": v(85.04, 209.64) * mm, "end": v(90.94, 196.22) * mm});
            skSolve(sketch);
        }
        {
            var Q0;
            Q0 = qSketchRegion(id + "F18", true);
            extrude(context, id + "F19", {"entities" : qUnion([Q0]), "operationType" : NewBodyOperationType.ADD, "depth" : 5.08 * mm});
        }
        {
            var Q0;
            Q0=makeQuery(id+"F17.opExtrude","SWEPT_BODY",BODY,{"disambiguationData":[OSD([sQuery(id+"F16.wireOp",EDGE,"KNlQa4Zo-YTXx-w4N4-aRN1-drF1v70HGVSZ"),sQuery(id+"F16.wireOp",EDGE,"E104"),sQuery(id+"F16.wireOp",EDGE,"FqjqoJdd-gPWH-Xghq-b061-MRI81XmJMNie"),sQuery(id+"F16.wireOp",EDGE,"fIdaUP2V-rCuL-g9az-AqTW-ZxU4SovSAGXS"),sQuery(id+"F16.wireOp",EDGE,"xGjuTvcU-3kij-0HJ7-qXFS-f4At5dvGbPoV"),sQuery(id+"F16.wireOp",EDGE,"AweFUQ5t-gSvw-yYcX-pN2m-7zr78jBIP70m"),sQuery(id+"F16.wireOp",EDGE,"E106"),sQuery(id+"F16.wireOp",EDGE,"E107"),sQuery(id+"F16.wireOp",EDGE,"E108"),sQuery(id+"F16.wireOp",EDGE,"E109"),sQuery(id+"F16.wireOp",EDGE,"E110"),sQuery(id+"F16.wireOp",EDGE,"E111"),sQuery(id+"F16.wireOp",EDGE,"E112"),sQuery(id+"F16.wireOp",EDGE,"E113"),sQuery(id+"F16.wireOp",EDGE,"E114"),sQuery(id+"F16.wireOp",EDGE,"E115"),sQuery(id+"F16.wireOp",EDGE,"E116"),sQuery(id+"F16.wireOp",EDGE,"E117"),sQuery(id+"F16.wireOp",EDGE,"E118"),sQuery(id+"F16.wireOp",EDGE,"E119"),sQuery(id+"F16.wireOp",EDGE,"E120"),sQuery(id+"F16.wireOp",EDGE,"E121"),sQuery(id+"F16.wireOp",EDGE,"E122"),sQuery(id+"F16.wireOp",EDGE,"S4ZgD4fj-wu3B-b9gq-MFdI-6nMHIDOnMf1b"),sQuery(id+"F16.wireOp",EDGE,"2MMLHgPb-Od2S-jgy6-R7KS-3pFeT9BqBlrX"),sQuery(id+"F16.wireOp",EDGE,"9zRfOSmV-DnoR-IQm2-8mvr-R97rpbvwHzC0"),sQuery(id+"F16.wireOp",EDGE,"5N0TxjvZ-mL3s-Sypx-gYDa-ILURxNQzjUeC"),sQuery(id+"F16.wireOp",EDGE,"E123"),sQuery(id+"F16.wireOp",EDGE,"E124"),sQuery(id+"F16.wireOp",EDGE,"E125"),sQuery(id+"F16.wireOp",EDGE,"E126"),sQuery(id+"F16.wireOp",EDGE,"E127"),sQuery(id+"F16.wireOp",EDGE,"E128"),sQuery(id+"F16.wireOp",EDGE,"E129"),sQuery(id+"F16.wireOp",EDGE,"E131"),sQuery(id+"F16.wireOp",EDGE,"E132"),sQuery(id+"F16.wireOp",EDGE,"E133"),sQuery(id+"F16.wireOp",EDGE,"E134"),sQuery(id+"F16.wireOp",EDGE,"E135.filletArc"),sQuery(id+"F16.wireOp",EDGE,"E136.filletArc"),sQuery(id+"F16.wireOp",EDGE,"E137"),sQuery(id+"F16.wireOp",EDGE,"E138"),sQuery(id+"F16.wireOp",EDGE,"E139"),sQuery(id+"F16.wireOp",EDGE,"E140.filletArc"),sQuery(id+"F16.wireOp",EDGE,"E141.filletArc"),sQuery(id+"F16.wireOp",EDGE,"E142"),sQuery(id+"F16.wireOp",EDGE,"E143"),sQuery(id+"F16.wireOp",EDGE,"E144"),sQuery(id+"F16.wireOp",EDGE,"bTRVcH6j-3HTp-rHIk-iP38-RX5fOa6IICLK"),sQuery(id+"F16.wireOp",EDGE,"ZxG8Ixeu-TiUJ-X6Ws-LEH0-SgtDoKyzScIO"),sQuery(id+"F16.wireOp",EDGE,"iqhDDctJ-DFI0-w93G-mWSZ-jod7B4hKst5q"),sQuery(id+"F16.wireOp",EDGE,"kJg86Nbg-BVFe-9bgW-d4b1-XLPkjMBWPouF"),sQuery(id+"F16.wireOp",EDGE,"vzD8kHnG-j6Yj-tT0k-EJiF-sAF0qJC3kBsM"),sQuery(id+"F16.wireOp",EDGE,"ATLLkzoR-xLp8-PK2h-xpL1-4FHkQ0npFU1p"),sQuery(id+"F16.wireOp",EDGE,"A9BTCMLA-84TM-lB5k-Eluh-QPGjXW7soWaE"),sQuery(id+"F16.wireOp",EDGE,"R5GvcQym-SsAj-qG7A-otxq-drPFPu247RhT"),sQuery(id+"F16.wireOp",EDGE,"KW7av8gp-Ffvi-hUdM-28wj-p3RSLdVNXCTe"),sQuery(id+"F16.wireOp",EDGE,"8fdd0ad8-850c-40ae-9457-b2188aafbfc6.filletArc"),sQuery(id+"F16.wireOp",EDGE,"b7d22ab5-fd41-4537-b8d2-879762634df6.filletArc"),sQuery(id+"F16.wireOp",EDGE,"18aa52c6-2d0c-4a72-a31e-9e2052208f85.filletArc"),sQuery(id+"F16.wireOp",EDGE,"1a89a74f-9219-4d13-8580-9d6571421a05.filletArc")])]});
            transform(context, id + "F20", {"entities" : qUnion([Q0]), "transformType" : TransformType.TRANSLATION_3D, "dx" : 292.1 * mm, "dy" : 0 * mm, "dz" : -273.05 * mm, "makeCopy" : true});
        }
        {
            var Q0;
            Q0=makeQuery(id+"F20.opPattern","COPY",BODY,{"derivedFrom":makeQuery(id+"F17.opExtrude","SWEPT_BODY",BODY,{"disambiguationData":[OSD([sQuery(id+"F16.wireOp",EDGE,"KNlQa4Zo-YTXx-w4N4-aRN1-drF1v70HGVSZ"),sQuery(id+"F16.wireOp",EDGE,"E104"),sQuery(id+"F16.wireOp",EDGE,"FqjqoJdd-gPWH-Xghq-b061-MRI81XmJMNie"),sQuery(id+"F16.wireOp",EDGE,"fIdaUP2V-rCuL-g9az-AqTW-ZxU4SovSAGXS"),sQuery(id+"F16.wireOp",EDGE,"xGjuTvcU-3kij-0HJ7-qXFS-f4At5dvGbPoV"),sQuery(id+"F16.wireOp",EDGE,"AweFUQ5t-gSvw-yYcX-pN2m-7zr78jBIP70m"),sQuery(id+"F16.wireOp",EDGE,"E106"),sQuery(id+"F16.wireOp",EDGE,"E107"),sQuery(id+"F16.wireOp",EDGE,"E108"),sQuery(id+"F16.wireOp",EDGE,"E109"),sQuery(id+"F16.wireOp",EDGE,"E110"),sQuery(id+"F16.wireOp",EDGE,"E111"),sQuery(id+"F16.wireOp",EDGE,"E112"),sQuery(id+"F16.wireOp",EDGE,"E113"),sQuery(id+"F16.wireOp",EDGE,"E114"),sQuery(id+"F16.wireOp",EDGE,"E115"),sQuery(id+"F16.wireOp",EDGE,"E116"),sQuery(id+"F16.wireOp",EDGE,"E117"),sQuery(id+"F16.wireOp",EDGE,"E118"),sQuery(id+"F16.wireOp",EDGE,"E119"),sQuery(id+"F16.wireOp",EDGE,"E120"),sQuery(id+"F16.wireOp",EDGE,"E121"),sQuery(id+"F16.wireOp",EDGE,"E122"),sQuery(id+"F16.wireOp",EDGE,"S4ZgD4fj-wu3B-b9gq-MFdI-6nMHIDOnMf1b"),sQuery(id+"F16.wireOp",EDGE,"2MMLHgPb-Od2S-jgy6-R7KS-3pFeT9BqBlrX"),sQuery(id+"F16.wireOp",EDGE,"9zRfOSmV-DnoR-IQm2-8mvr-R97rpbvwHzC0"),sQuery(id+"F16.wireOp",EDGE,"5N0TxjvZ-mL3s-Sypx-gYDa-ILURxNQzjUeC"),sQuery(id+"F16.wireOp",EDGE,"E123"),sQuery(id+"F16.wireOp",EDGE,"E124"),sQuery(id+"F16.wireOp",EDGE,"E125"),sQuery(id+"F16.wireOp",EDGE,"E126"),sQuery(id+"F16.wireOp",EDGE,"E127"),sQuery(id+"F16.wireOp",EDGE,"E128"),sQuery(id+"F16.wireOp",EDGE,"E129"),sQuery(id+"F16.wireOp",EDGE,"E131"),sQuery(id+"F16.wireOp",EDGE,"E132"),sQuery(id+"F16.wireOp",EDGE,"E133"),sQuery(id+"F16.wireOp",EDGE,"E134"),sQuery(id+"F16.wireOp",EDGE,"E135.filletArc"),sQuery(id+"F16.wireOp",EDGE,"E136.filletArc"),sQuery(id+"F16.wireOp",EDGE,"E137"),sQuery(id+"F16.wireOp",EDGE,"E138"),sQuery(id+"F16.wireOp",EDGE,"E139"),sQuery(id+"F16.wireOp",EDGE,"E140.filletArc"),sQuery(id+"F16.wireOp",EDGE,"E141.filletArc"),sQuery(id+"F16.wireOp",EDGE,"E142"),sQuery(id+"F16.wireOp",EDGE,"E143"),sQuery(id+"F16.wireOp",EDGE,"E144"),sQuery(id+"F16.wireOp",EDGE,"bTRVcH6j-3HTp-rHIk-iP38-RX5fOa6IICLK"),sQuery(id+"F16.wireOp",EDGE,"ZxG8Ixeu-TiUJ-X6Ws-LEH0-SgtDoKyzScIO"),sQuery(id+"F16.wireOp",EDGE,"iqhDDctJ-DFI0-w93G-mWSZ-jod7B4hKst5q"),sQuery(id+"F16.wireOp",EDGE,"kJg86Nbg-BVFe-9bgW-d4b1-XLPkjMBWPouF"),sQuery(id+"F16.wireOp",EDGE,"vzD8kHnG-j6Yj-tT0k-EJiF-sAF0qJC3kBsM"),sQuery(id+"F16.wireOp",EDGE,"ATLLkzoR-xLp8-PK2h-xpL1-4FHkQ0npFU1p"),sQuery(id+"F16.wireOp",EDGE,"A9BTCMLA-84TM-lB5k-Eluh-QPGjXW7soWaE"),sQuery(id+"F16.wireOp",EDGE,"R5GvcQym-SsAj-qG7A-otxq-drPFPu247RhT"),sQuery(id+"F16.wireOp",EDGE,"KW7av8gp-Ffvi-hUdM-28wj-p3RSLdVNXCTe"),sQuery(id+"F16.wireOp",EDGE,"8fdd0ad8-850c-40ae-9457-b2188aafbfc6.filletArc"),sQuery(id+"F16.wireOp",EDGE,"b7d22ab5-fd41-4537-b8d2-879762634df6.filletArc"),sQuery(id+"F16.wireOp",EDGE,"18aa52c6-2d0c-4a72-a31e-9e2052208f85.filletArc"),sQuery(id+"F16.wireOp",EDGE,"1a89a74f-9219-4d13-8580-9d6571421a05.filletArc")])]}),"instanceName":"1"});
            transform(context, id + "F21", {"entities" : qUnion([Q0]), "transformType" : TransformType.TRANSLATION_3D, "dx" : 0 * mm, "dy" : 0 * mm, "dz" : -177.8 * mm, "makeCopy" : true});
        }
        {
            var Q0;
            Q0=makeQuery(id+"F21.opPattern","COPY",BODY,{"derivedFrom":makeQuery(id+"F20.opPattern","COPY",BODY,{"derivedFrom":makeQuery(id+"F17.opExtrude","SWEPT_BODY",BODY,{"disambiguationData":[OSD([sQuery(id+"F16.wireOp",EDGE,"KNlQa4Zo-YTXx-w4N4-aRN1-drF1v70HGVSZ"),sQuery(id+"F16.wireOp",EDGE,"E104"),sQuery(id+"F16.wireOp",EDGE,"FqjqoJdd-gPWH-Xghq-b061-MRI81XmJMNie"),sQuery(id+"F16.wireOp",EDGE,"fIdaUP2V-rCuL-g9az-AqTW-ZxU4SovSAGXS"),sQuery(id+"F16.wireOp",EDGE,"xGjuTvcU-3kij-0HJ7-qXFS-f4At5dvGbPoV"),sQuery(id+"F16.wireOp",EDGE,"AweFUQ5t-gSvw-yYcX-pN2m-7zr78jBIP70m"),sQuery(id+"F16.wireOp",EDGE,"E106"),sQuery(id+"F16.wireOp",EDGE,"E107"),sQuery(id+"F16.wireOp",EDGE,"E108"),sQuery(id+"F16.wireOp",EDGE,"E109"),sQuery(id+"F16.wireOp",EDGE,"E110"),sQuery(id+"F16.wireOp",EDGE,"E111"),sQuery(id+"F16.wireOp",EDGE,"E112"),sQuery(id+"F16.wireOp",EDGE,"E113"),sQuery(id+"F16.wireOp",EDGE,"E114"),sQuery(id+"F16.wireOp",EDGE,"E115"),sQuery(id+"F16.wireOp",EDGE,"E116"),sQuery(id+"F16.wireOp",EDGE,"E117"),sQuery(id+"F16.wireOp",EDGE,"E118"),sQuery(id+"F16.wireOp",EDGE,"E119"),sQuery(id+"F16.wireOp",EDGE,"E120"),sQuery(id+"F16.wireOp",EDGE,"E121"),sQuery(id+"F16.wireOp",EDGE,"E122"),sQuery(id+"F16.wireOp",EDGE,"S4ZgD4fj-wu3B-b9gq-MFdI-6nMHIDOnMf1b"),sQuery(id+"F16.wireOp",EDGE,"2MMLHgPb-Od2S-jgy6-R7KS-3pFeT9BqBlrX"),sQuery(id+"F16.wireOp",EDGE,"9zRfOSmV-DnoR-IQm2-8mvr-R97rpbvwHzC0"),sQuery(id+"F16.wireOp",EDGE,"5N0TxjvZ-mL3s-Sypx-gYDa-ILURxNQzjUeC"),sQuery(id+"F16.wireOp",EDGE,"E123"),sQuery(id+"F16.wireOp",EDGE,"E124"),sQuery(id+"F16.wireOp",EDGE,"E125"),sQuery(id+"F16.wireOp",EDGE,"E126"),sQuery(id+"F16.wireOp",EDGE,"E127"),sQuery(id+"F16.wireOp",EDGE,"E128"),sQuery(id+"F16.wireOp",EDGE,"E129"),sQuery(id+"F16.wireOp",EDGE,"E131"),sQuery(id+"F16.wireOp",EDGE,"E132"),sQuery(id+"F16.wireOp",EDGE,"E133"),sQuery(id+"F16.wireOp",EDGE,"E134"),sQuery(id+"F16.wireOp",EDGE,"E135.filletArc"),sQuery(id+"F16.wireOp",EDGE,"E136.filletArc"),sQuery(id+"F16.wireOp",EDGE,"E137"),sQuery(id+"F16.wireOp",EDGE,"E138"),sQuery(id+"F16.wireOp",EDGE,"E139"),sQuery(id+"F16.wireOp",EDGE,"E140.filletArc"),sQuery(id+"F16.wireOp",EDGE,"E141.filletArc"),sQuery(id+"F16.wireOp",EDGE,"E142"),sQuery(id+"F16.wireOp",EDGE,"E143"),sQuery(id+"F16.wireOp",EDGE,"E144"),sQuery(id+"F16.wireOp",EDGE,"bTRVcH6j-3HTp-rHIk-iP38-RX5fOa6IICLK"),sQuery(id+"F16.wireOp",EDGE,"ZxG8Ixeu-TiUJ-X6Ws-LEH0-SgtDoKyzScIO"),sQuery(id+"F16.wireOp",EDGE,"iqhDDctJ-DFI0-w93G-mWSZ-jod7B4hKst5q"),sQuery(id+"F16.wireOp",EDGE,"kJg86Nbg-BVFe-9bgW-d4b1-XLPkjMBWPouF"),sQuery(id+"F16.wireOp",EDGE,"vzD8kHnG-j6Yj-tT0k-EJiF-sAF0qJC3kBsM"),sQuery(id+"F16.wireOp",EDGE,"ATLLkzoR-xLp8-PK2h-xpL1-4FHkQ0npFU1p"),sQuery(id+"F16.wireOp",EDGE,"A9BTCMLA-84TM-lB5k-Eluh-QPGjXW7soWaE"),sQuery(id+"F16.wireOp",EDGE,"R5GvcQym-SsAj-qG7A-otxq-drPFPu247RhT"),sQuery(id+"F16.wireOp",EDGE,"KW7av8gp-Ffvi-hUdM-28wj-p3RSLdVNXCTe"),sQuery(id+"F16.wireOp",EDGE,"8fdd0ad8-850c-40ae-9457-b2188aafbfc6.filletArc"),sQuery(id+"F16.wireOp",EDGE,"b7d22ab5-fd41-4537-b8d2-879762634df6.filletArc"),sQuery(id+"F16.wireOp",EDGE,"18aa52c6-2d0c-4a72-a31e-9e2052208f85.filletArc"),sQuery(id+"F16.wireOp",EDGE,"1a89a74f-9219-4d13-8580-9d6571421a05.filletArc")])]}),"instanceName":"1"}),"instanceName":"1"});
            transform(context, id + "F22", {"entities" : qUnion([Q0]), "transformType" : TransformType.TRANSLATION_3D, "dx" : 241.3 * mm, "dy" : 0 * mm, "dz" : 0 * mm, "makeCopy" : true});
        }
        {
            var Q0;
            Q0=makeQuery(id+"F22.opPattern","COPY",BODY,{"derivedFrom":makeQuery(id+"F21.opPattern","COPY",BODY,{"derivedFrom":makeQuery(id+"F20.opPattern","COPY",BODY,{"derivedFrom":makeQuery(id+"F17.opExtrude","SWEPT_BODY",BODY,{"disambiguationData":[OSD([sQuery(id+"F16.wireOp",EDGE,"KNlQa4Zo-YTXx-w4N4-aRN1-drF1v70HGVSZ"),sQuery(id+"F16.wireOp",EDGE,"E104"),sQuery(id+"F16.wireOp",EDGE,"FqjqoJdd-gPWH-Xghq-b061-MRI81XmJMNie"),sQuery(id+"F16.wireOp",EDGE,"fIdaUP2V-rCuL-g9az-AqTW-ZxU4SovSAGXS"),sQuery(id+"F16.wireOp",EDGE,"xGjuTvcU-3kij-0HJ7-qXFS-f4At5dvGbPoV"),sQuery(id+"F16.wireOp",EDGE,"AweFUQ5t-gSvw-yYcX-pN2m-7zr78jBIP70m"),sQuery(id+"F16.wireOp",EDGE,"E106"),sQuery(id+"F16.wireOp",EDGE,"E107"),sQuery(id+"F16.wireOp",EDGE,"E108"),sQuery(id+"F16.wireOp",EDGE,"E109"),sQuery(id+"F16.wireOp",EDGE,"E110"),sQuery(id+"F16.wireOp",EDGE,"E111"),sQuery(id+"F16.wireOp",EDGE,"E112"),sQuery(id+"F16.wireOp",EDGE,"E113"),sQuery(id+"F16.wireOp",EDGE,"E114"),sQuery(id+"F16.wireOp",EDGE,"E115"),sQuery(id+"F16.wireOp",EDGE,"E116"),sQuery(id+"F16.wireOp",EDGE,"E117"),sQuery(id+"F16.wireOp",EDGE,"E118"),sQuery(id+"F16.wireOp",EDGE,"E119"),sQuery(id+"F16.wireOp",EDGE,"E120"),sQuery(id+"F16.wireOp",EDGE,"E121"),sQuery(id+"F16.wireOp",EDGE,"E122"),sQuery(id+"F16.wireOp",EDGE,"S4ZgD4fj-wu3B-b9gq-MFdI-6nMHIDOnMf1b"),sQuery(id+"F16.wireOp",EDGE,"2MMLHgPb-Od2S-jgy6-R7KS-3pFeT9BqBlrX"),sQuery(id+"F16.wireOp",EDGE,"9zRfOSmV-DnoR-IQm2-8mvr-R97rpbvwHzC0"),sQuery(id+"F16.wireOp",EDGE,"5N0TxjvZ-mL3s-Sypx-gYDa-ILURxNQzjUeC"),sQuery(id+"F16.wireOp",EDGE,"E123"),sQuery(id+"F16.wireOp",EDGE,"E124"),sQuery(id+"F16.wireOp",EDGE,"E125"),sQuery(id+"F16.wireOp",EDGE,"E126"),sQuery(id+"F16.wireOp",EDGE,"E127"),sQuery(id+"F16.wireOp",EDGE,"E128"),sQuery(id+"F16.wireOp",EDGE,"E129"),sQuery(id+"F16.wireOp",EDGE,"E131"),sQuery(id+"F16.wireOp",EDGE,"E132"),sQuery(id+"F16.wireOp",EDGE,"E133"),sQuery(id+"F16.wireOp",EDGE,"E134"),sQuery(id+"F16.wireOp",EDGE,"E135.filletArc"),sQuery(id+"F16.wireOp",EDGE,"E136.filletArc"),sQuery(id+"F16.wireOp",EDGE,"E137"),sQuery(id+"F16.wireOp",EDGE,"E138"),sQuery(id+"F16.wireOp",EDGE,"E139"),sQuery(id+"F16.wireOp",EDGE,"E140.filletArc"),sQuery(id+"F16.wireOp",EDGE,"E141.filletArc"),sQuery(id+"F16.wireOp",EDGE,"E142"),sQuery(id+"F16.wireOp",EDGE,"E143"),sQuery(id+"F16.wireOp",EDGE,"E144"),sQuery(id+"F16.wireOp",EDGE,"bTRVcH6j-3HTp-rHIk-iP38-RX5fOa6IICLK"),sQuery(id+"F16.wireOp",EDGE,"ZxG8Ixeu-TiUJ-X6Ws-LEH0-SgtDoKyzScIO"),sQuery(id+"F16.wireOp",EDGE,"iqhDDctJ-DFI0-w93G-mWSZ-jod7B4hKst5q"),sQuery(id+"F16.wireOp",EDGE,"kJg86Nbg-BVFe-9bgW-d4b1-XLPkjMBWPouF"),sQuery(id+"F16.wireOp",EDGE,"vzD8kHnG-j6Yj-tT0k-EJiF-sAF0qJC3kBsM"),sQuery(id+"F16.wireOp",EDGE,"ATLLkzoR-xLp8-PK2h-xpL1-4FHkQ0npFU1p"),sQuery(id+"F16.wireOp",EDGE,"A9BTCMLA-84TM-lB5k-Eluh-QPGjXW7soWaE"),sQuery(id+"F16.wireOp",EDGE,"R5GvcQym-SsAj-qG7A-otxq-drPFPu247RhT"),sQuery(id+"F16.wireOp",EDGE,"KW7av8gp-Ffvi-hUdM-28wj-p3RSLdVNXCTe"),sQuery(id+"F16.wireOp",EDGE,"8fdd0ad8-850c-40ae-9457-b2188aafbfc6.filletArc"),sQuery(id+"F16.wireOp",EDGE,"b7d22ab5-fd41-4537-b8d2-879762634df6.filletArc"),sQuery(id+"F16.wireOp",EDGE,"18aa52c6-2d0c-4a72-a31e-9e2052208f85.filletArc"),sQuery(id+"F16.wireOp",EDGE,"1a89a74f-9219-4d13-8580-9d6571421a05.filletArc")])]}),"instanceName":"1"}),"instanceName":"1"}),"instanceName":"1"});
            transform(context, id + "F23", {"entities" : qUnion([Q0]), "transformType" : TransformType.TRANSLATION_3D, "dx" : 0 * mm, "dy" : 0 * mm, "dz" : 158.75 * mm, "makeCopy" : true});
        }
        {
            var Q0;
            Q0=makeQuery(id+"F23.opPattern","COPY",BODY,{"derivedFrom":makeQuery(id+"F22.opPattern","COPY",BODY,{"derivedFrom":makeQuery(id+"F21.opPattern","COPY",BODY,{"derivedFrom":makeQuery(id+"F20.opPattern","COPY",BODY,{"derivedFrom":makeQuery(id+"F17.opExtrude","SWEPT_BODY",BODY,{"disambiguationData":[OSD([sQuery(id+"F16.wireOp",EDGE,"KNlQa4Zo-YTXx-w4N4-aRN1-drF1v70HGVSZ"),sQuery(id+"F16.wireOp",EDGE,"E104"),sQuery(id+"F16.wireOp",EDGE,"FqjqoJdd-gPWH-Xghq-b061-MRI81XmJMNie"),sQuery(id+"F16.wireOp",EDGE,"fIdaUP2V-rCuL-g9az-AqTW-ZxU4SovSAGXS"),sQuery(id+"F16.wireOp",EDGE,"xGjuTvcU-3kij-0HJ7-qXFS-f4At5dvGbPoV"),sQuery(id+"F16.wireOp",EDGE,"AweFUQ5t-gSvw-yYcX-pN2m-7zr78jBIP70m"),sQuery(id+"F16.wireOp",EDGE,"E106"),sQuery(id+"F16.wireOp",EDGE,"E107"),sQuery(id+"F16.wireOp",EDGE,"E108"),sQuery(id+"F16.wireOp",EDGE,"E109"),sQuery(id+"F16.wireOp",EDGE,"E110"),sQuery(id+"F16.wireOp",EDGE,"E111"),sQuery(id+"F16.wireOp",EDGE,"E112"),sQuery(id+"F16.wireOp",EDGE,"E113"),sQuery(id+"F16.wireOp",EDGE,"E114"),sQuery(id+"F16.wireOp",EDGE,"E115"),sQuery(id+"F16.wireOp",EDGE,"E116"),sQuery(id+"F16.wireOp",EDGE,"E117"),sQuery(id+"F16.wireOp",EDGE,"E118"),sQuery(id+"F16.wireOp",EDGE,"E119"),sQuery(id+"F16.wireOp",EDGE,"E120"),sQuery(id+"F16.wireOp",EDGE,"E121"),sQuery(id+"F16.wireOp",EDGE,"E122"),sQuery(id+"F16.wireOp",EDGE,"S4ZgD4fj-wu3B-b9gq-MFdI-6nMHIDOnMf1b"),sQuery(id+"F16.wireOp",EDGE,"2MMLHgPb-Od2S-jgy6-R7KS-3pFeT9BqBlrX"),sQuery(id+"F16.wireOp",EDGE,"9zRfOSmV-DnoR-IQm2-8mvr-R97rpbvwHzC0"),sQuery(id+"F16.wireOp",EDGE,"5N0TxjvZ-mL3s-Sypx-gYDa-ILURxNQzjUeC"),sQuery(id+"F16.wireOp",EDGE,"E123"),sQuery(id+"F16.wireOp",EDGE,"E124"),sQuery(id+"F16.wireOp",EDGE,"E125"),sQuery(id+"F16.wireOp",EDGE,"E126"),sQuery(id+"F16.wireOp",EDGE,"E127"),sQuery(id+"F16.wireOp",EDGE,"E128"),sQuery(id+"F16.wireOp",EDGE,"E129"),sQuery(id+"F16.wireOp",EDGE,"E131"),sQuery(id+"F16.wireOp",EDGE,"E132"),sQuery(id+"F16.wireOp",EDGE,"E133"),sQuery(id+"F16.wireOp",EDGE,"E134"),sQuery(id+"F16.wireOp",EDGE,"E135.filletArc"),sQuery(id+"F16.wireOp",EDGE,"E136.filletArc"),sQuery(id+"F16.wireOp",EDGE,"E137"),sQuery(id+"F16.wireOp",EDGE,"E138"),sQuery(id+"F16.wireOp",EDGE,"E139"),sQuery(id+"F16.wireOp",EDGE,"E140.filletArc"),sQuery(id+"F16.wireOp",EDGE,"E141.filletArc"),sQuery(id+"F16.wireOp",EDGE,"E142"),sQuery(id+"F16.wireOp",EDGE,"E143"),sQuery(id+"F16.wireOp",EDGE,"E144"),sQuery(id+"F16.wireOp",EDGE,"bTRVcH6j-3HTp-rHIk-iP38-RX5fOa6IICLK"),sQuery(id+"F16.wireOp",EDGE,"ZxG8Ixeu-TiUJ-X6Ws-LEH0-SgtDoKyzScIO"),sQuery(id+"F16.wireOp",EDGE,"iqhDDctJ-DFI0-w93G-mWSZ-jod7B4hKst5q"),sQuery(id+"F16.wireOp",EDGE,"kJg86Nbg-BVFe-9bgW-d4b1-XLPkjMBWPouF"),sQuery(id+"F16.wireOp",EDGE,"vzD8kHnG-j6Yj-tT0k-EJiF-sAF0qJC3kBsM"),sQuery(id+"F16.wireOp",EDGE,"ATLLkzoR-xLp8-PK2h-xpL1-4FHkQ0npFU1p"),sQuery(id+"F16.wireOp",EDGE,"A9BTCMLA-84TM-lB5k-Eluh-QPGjXW7soWaE"),sQuery(id+"F16.wireOp",EDGE,"R5GvcQym-SsAj-qG7A-otxq-drPFPu247RhT"),sQuery(id+"F16.wireOp",EDGE,"KW7av8gp-Ffvi-hUdM-28wj-p3RSLdVNXCTe"),sQuery(id+"F16.wireOp",EDGE,"8fdd0ad8-850c-40ae-9457-b2188aafbfc6.filletArc"),sQuery(id+"F16.wireOp",EDGE,"b7d22ab5-fd41-4537-b8d2-879762634df6.filletArc"),sQuery(id+"F16.wireOp",EDGE,"18aa52c6-2d0c-4a72-a31e-9e2052208f85.filletArc"),sQuery(id+"F16.wireOp",EDGE,"1a89a74f-9219-4d13-8580-9d6571421a05.filletArc")])]}),"instanceName":"1"}),"instanceName":"1"}),"instanceName":"1"}),"instanceName":"1"});
            transform(context, id + "F24", {"entities" : qUnion([Q0]), "transformType" : TransformType.TRANSLATION_3D, "dx" : 234.95 * mm, "dy" : 0 * mm, "dz" : 0 * mm, "makeCopy" : true});
        }
    });
